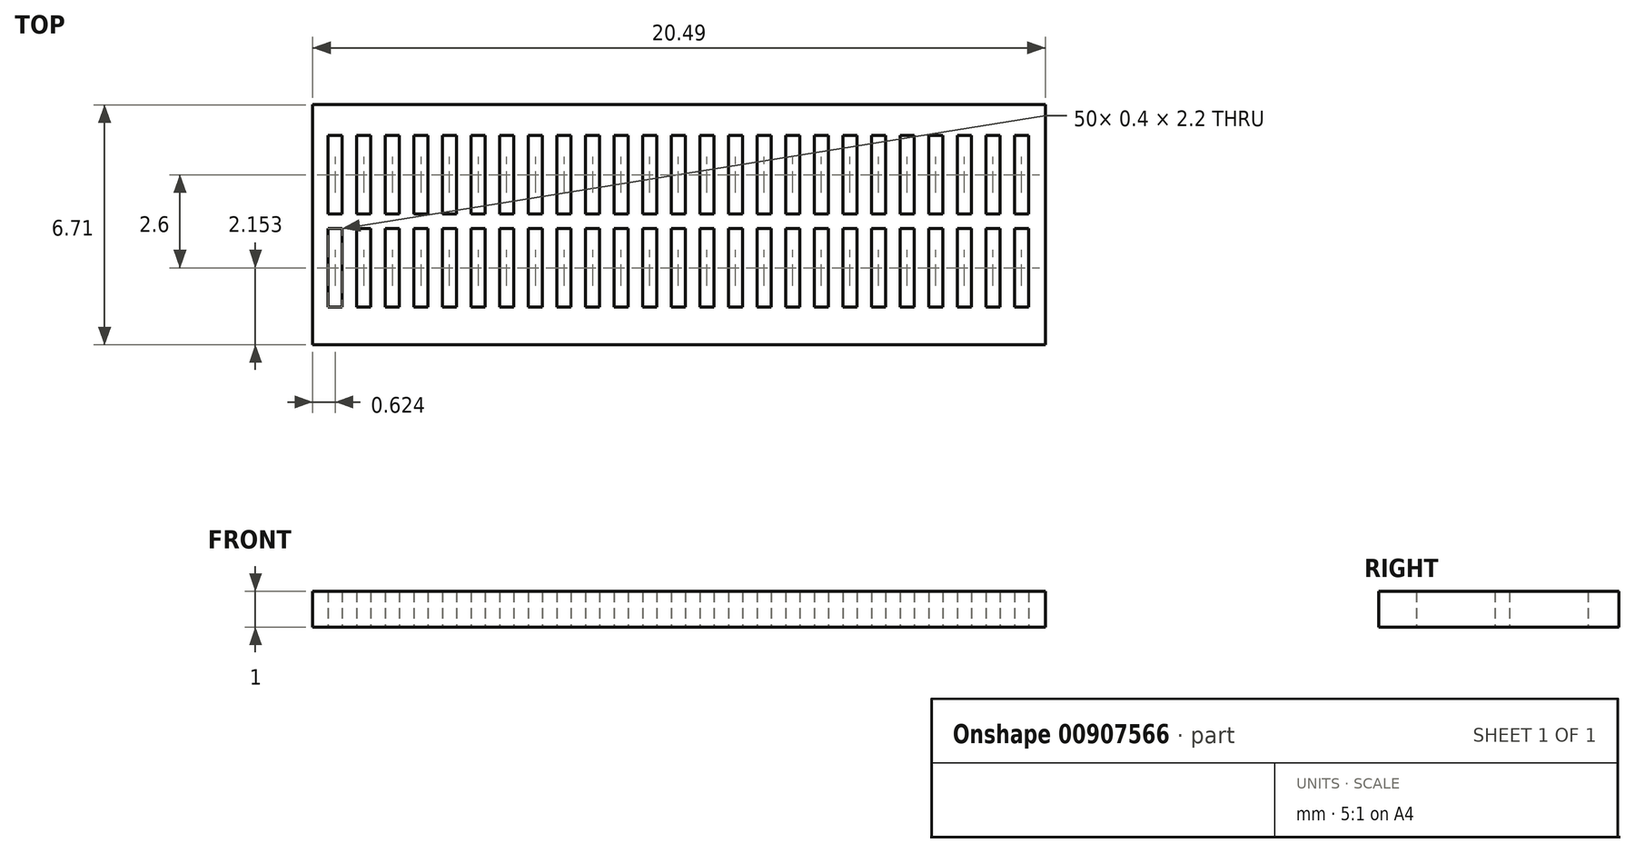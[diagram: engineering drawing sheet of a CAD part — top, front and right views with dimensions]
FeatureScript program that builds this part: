
annotation { "Feature Type Name" : "Feature", "Feature Type Description" : "" }
export const myFeature = defineFeature(function(context is Context, id is Id, definition is map)
    precondition{}
    {
        {
            var Q0;
            Q0=qCreatedBy(makeId("Top.planeOp"),FACE);
            var sketch = newSketch(context, id + "F0", { "sketchPlane" : qUnion([Q0])});
            skLineSegment(sketch, "E0.bottom", {"start": v(-8.03, 0) * mm, "end": v(-7.53, 0) * mm});
            skLineSegment(sketch, "E0.top", {"start": v(-8.03, 2.2) * mm, "end": v(-7.53, 2.2) * mm});
            skLineSegment(sketch, "E0.left", {"start": v(-8.03, 0) * mm, "end": v(-8.03, 2.2) * mm});
            skLineSegment(sketch, "E0.right", {"start": v(-7.53, 0) * mm, "end": v(-7.53, 2.2) * mm});
            skLineSegment(sketch, "E1.0.1.0", {"start": v(-8.03, -4.6) * mm, "end": v(-8.03, -2.4) * mm});
            skLineSegment(sketch, "E1.0.1.1", {"start": v(-8.03, -2.4) * mm, "end": v(-7.53, -2.4) * mm});
            skLineSegment(sketch, "E1.0.1.2", {"start": v(-7.53, -4.6) * mm, "end": v(-7.53, -2.4) * mm});
            skLineSegment(sketch, "E1.0.1.3", {"start": v(-8.03, -4.6) * mm, "end": v(-7.53, -4.6) * mm});
            skLineSegment(sketch, "E1.1.0.0", {"start": v(-7.23, 0) * mm, "end": v(-7.23, 2.2) * mm});
            skLineSegment(sketch, "E1.1.0.1", {"start": v(-7.23, 2.2) * mm, "end": v(-6.73, 2.2) * mm});
            skLineSegment(sketch, "E1.1.0.2", {"start": v(-6.73, 0) * mm, "end": v(-6.73, 2.2) * mm});
            skLineSegment(sketch, "E1.1.0.3", {"start": v(-7.23, 0) * mm, "end": v(-6.73, 0) * mm});
            skLineSegment(sketch, "E1.1.1.0", {"start": v(-7.23, -4.6) * mm, "end": v(-7.23, -2.4) * mm});
            skLineSegment(sketch, "E1.1.1.1", {"start": v(-7.23, -2.4) * mm, "end": v(-6.73, -2.4) * mm});
            skLineSegment(sketch, "E1.1.1.2", {"start": v(-6.73, -4.6) * mm, "end": v(-6.73, -2.4) * mm});
            skLineSegment(sketch, "E1.1.1.3", {"start": v(-7.23, -4.6) * mm, "end": v(-6.73, -4.6) * mm});
            skLineSegment(sketch, "E1.2.0.0", {"start": v(-6.43, 0) * mm, "end": v(-6.43, 2.2) * mm});
            skLineSegment(sketch, "E1.2.0.1", {"start": v(-6.43, 2.2) * mm, "end": v(-5.93, 2.2) * mm});
            skLineSegment(sketch, "E1.2.0.2", {"start": v(-5.93, 0) * mm, "end": v(-5.93, 2.2) * mm});
            skLineSegment(sketch, "E1.2.0.3", {"start": v(-6.43, 0) * mm, "end": v(-5.93, 0) * mm});
            skLineSegment(sketch, "E1.2.1.0", {"start": v(-6.43, -4.6) * mm, "end": v(-6.43, -2.4) * mm});
            skLineSegment(sketch, "E1.2.1.1", {"start": v(-6.43, -2.4) * mm, "end": v(-5.93, -2.4) * mm});
            skLineSegment(sketch, "E1.2.1.2", {"start": v(-5.93, -4.6) * mm, "end": v(-5.93, -2.4) * mm});
            skLineSegment(sketch, "E1.2.1.3", {"start": v(-6.43, -4.6) * mm, "end": v(-5.93, -4.6) * mm});
            skLineSegment(sketch, "E1.3.0.0", {"start": v(-5.63, 0) * mm, "end": v(-5.63, 2.2) * mm});
            skLineSegment(sketch, "E1.3.0.1", {"start": v(-5.63, 2.2) * mm, "end": v(-5.13, 2.2) * mm});
            skLineSegment(sketch, "E1.3.0.2", {"start": v(-5.13, 0) * mm, "end": v(-5.13, 2.2) * mm});
            skLineSegment(sketch, "E1.3.0.3", {"start": v(-5.63, 0) * mm, "end": v(-5.13, 0) * mm});
            skLineSegment(sketch, "E1.3.1.0", {"start": v(-5.63, -4.6) * mm, "end": v(-5.63, -2.4) * mm});
            skLineSegment(sketch, "E1.3.1.1", {"start": v(-5.63, -2.4) * mm, "end": v(-5.13, -2.4) * mm});
            skLineSegment(sketch, "E1.3.1.2", {"start": v(-5.13, -4.6) * mm, "end": v(-5.13, -2.4) * mm});
            skLineSegment(sketch, "E1.3.1.3", {"start": v(-5.63, -4.6) * mm, "end": v(-5.13, -4.6) * mm});
            skLineSegment(sketch, "E1.4.0.0", {"start": v(-4.83, 0) * mm, "end": v(-4.83, 2.2) * mm});
            skLineSegment(sketch, "E1.4.0.1", {"start": v(-4.83, 2.2) * mm, "end": v(-4.33, 2.2) * mm});
            skLineSegment(sketch, "E1.4.0.2", {"start": v(-4.33, 0) * mm, "end": v(-4.33, 2.2) * mm});
            skLineSegment(sketch, "E1.4.0.3", {"start": v(-4.83, 0) * mm, "end": v(-4.33, 0) * mm});
            skLineSegment(sketch, "E1.4.1.0", {"start": v(-4.83, -4.6) * mm, "end": v(-4.83, -2.4) * mm});
            skLineSegment(sketch, "E1.4.1.1", {"start": v(-4.83, -2.4) * mm, "end": v(-4.33, -2.4) * mm});
            skLineSegment(sketch, "E1.4.1.2", {"start": v(-4.33, -4.6) * mm, "end": v(-4.33, -2.4) * mm});
            skLineSegment(sketch, "E1.4.1.3", {"start": v(-4.83, -4.6) * mm, "end": v(-4.33, -4.6) * mm});
            skLineSegment(sketch, "E1.5.0.0", {"start": v(-4.03, 0) * mm, "end": v(-4.03, 2.2) * mm});
            skLineSegment(sketch, "E1.5.0.1", {"start": v(-4.03, 2.2) * mm, "end": v(-3.53, 2.2) * mm});
            skLineSegment(sketch, "E1.5.0.2", {"start": v(-3.53, 0) * mm, "end": v(-3.53, 2.2) * mm});
            skLineSegment(sketch, "E1.5.0.3", {"start": v(-4.03, 0) * mm, "end": v(-3.53, 0) * mm});
            skLineSegment(sketch, "E1.5.1.0", {"start": v(-4.03, -4.6) * mm, "end": v(-4.03, -2.4) * mm});
            skLineSegment(sketch, "E1.5.1.1", {"start": v(-4.03, -2.4) * mm, "end": v(-3.53, -2.4) * mm});
            skLineSegment(sketch, "E1.5.1.2", {"start": v(-3.53, -4.6) * mm, "end": v(-3.53, -2.4) * mm});
            skLineSegment(sketch, "E1.5.1.3", {"start": v(-4.03, -4.6) * mm, "end": v(-3.53, -4.6) * mm});
            skLineSegment(sketch, "E1.6.0.0", {"start": v(-3.23, 0) * mm, "end": v(-3.23, 2.2) * mm});
            skLineSegment(sketch, "E1.6.0.1", {"start": v(-3.23, 2.2) * mm, "end": v(-2.73, 2.2) * mm});
            skLineSegment(sketch, "E1.6.0.2", {"start": v(-2.73, 0) * mm, "end": v(-2.73, 2.2) * mm});
            skLineSegment(sketch, "E1.6.0.3", {"start": v(-3.23, 0) * mm, "end": v(-2.73, 0) * mm});
            skLineSegment(sketch, "E1.6.1.0", {"start": v(-3.23, -4.6) * mm, "end": v(-3.23, -2.4) * mm});
            skLineSegment(sketch, "E1.6.1.1", {"start": v(-3.23, -2.4) * mm, "end": v(-2.73, -2.4) * mm});
            skLineSegment(sketch, "E1.6.1.2", {"start": v(-2.73, -4.6) * mm, "end": v(-2.73, -2.4) * mm});
            skLineSegment(sketch, "E1.6.1.3", {"start": v(-3.23, -4.6) * mm, "end": v(-2.73, -4.6) * mm});
            skLineSegment(sketch, "E1.7.0.0", {"start": v(-2.43, 0) * mm, "end": v(-2.43, 2.2) * mm});
            skLineSegment(sketch, "E1.7.0.1", {"start": v(-2.43, 2.2) * mm, "end": v(-1.93, 2.2) * mm});
            skLineSegment(sketch, "E1.7.0.2", {"start": v(-1.93, 0) * mm, "end": v(-1.93, 2.2) * mm});
            skLineSegment(sketch, "E1.7.0.3", {"start": v(-2.43, 0) * mm, "end": v(-1.93, 0) * mm});
            skLineSegment(sketch, "E1.7.1.0", {"start": v(-2.43, -4.6) * mm, "end": v(-2.43, -2.4) * mm});
            skLineSegment(sketch, "E1.7.1.1", {"start": v(-2.43, -2.4) * mm, "end": v(-1.93, -2.4) * mm});
            skLineSegment(sketch, "E1.7.1.2", {"start": v(-1.93, -4.6) * mm, "end": v(-1.93, -2.4) * mm});
            skLineSegment(sketch, "E1.7.1.3", {"start": v(-2.43, -4.6) * mm, "end": v(-1.93, -4.6) * mm});
            skLineSegment(sketch, "E1.8.0.0", {"start": v(-1.63, 0) * mm, "end": v(-1.63, 2.2) * mm});
            skLineSegment(sketch, "E1.8.0.1", {"start": v(-1.63, 2.2) * mm, "end": v(-1.13, 2.2) * mm});
            skLineSegment(sketch, "E1.8.0.2", {"start": v(-1.13, 0) * mm, "end": v(-1.13, 2.2) * mm});
            skLineSegment(sketch, "E1.8.0.3", {"start": v(-1.63, 0) * mm, "end": v(-1.13, 0) * mm});
            skLineSegment(sketch, "E1.8.1.0", {"start": v(-1.63, -4.6) * mm, "end": v(-1.63, -2.4) * mm});
            skLineSegment(sketch, "E1.8.1.1", {"start": v(-1.63, -2.4) * mm, "end": v(-1.13, -2.4) * mm});
            skLineSegment(sketch, "E1.8.1.2", {"start": v(-1.13, -4.6) * mm, "end": v(-1.13, -2.4) * mm});
            skLineSegment(sketch, "E1.8.1.3", {"start": v(-1.63, -4.6) * mm, "end": v(-1.13, -4.6) * mm});
            skLineSegment(sketch, "E1.9.0.0", {"start": v(-0.83, 0) * mm, "end": v(-0.83, 2.2) * mm});
            skLineSegment(sketch, "E1.9.0.1", {"start": v(-0.83, 2.2) * mm, "end": v(-0.33, 2.2) * mm});
            skLineSegment(sketch, "E1.9.0.2", {"start": v(-0.33, 0) * mm, "end": v(-0.33, 2.2) * mm});
            skLineSegment(sketch, "E1.9.0.3", {"start": v(-0.83, 0) * mm, "end": v(-0.33, 0) * mm});
            skLineSegment(sketch, "E1.9.1.0", {"start": v(-0.83, -4.6) * mm, "end": v(-0.83, -2.4) * mm});
            skLineSegment(sketch, "E1.9.1.1", {"start": v(-0.83, -2.4) * mm, "end": v(-0.33, -2.4) * mm});
            skLineSegment(sketch, "E1.9.1.2", {"start": v(-0.33, -4.6) * mm, "end": v(-0.33, -2.4) * mm});
            skLineSegment(sketch, "E1.9.1.3", {"start": v(-0.83, -4.6) * mm, "end": v(-0.33, -4.6) * mm});
            skLineSegment(sketch, "E1.10.0.0", {"start": v(-0.03, 0) * mm, "end": v(-0.03, 2.2) * mm});
            skLineSegment(sketch, "E1.10.0.1", {"start": v(-0.03, 2.2) * mm, "end": v(0.47, 2.2) * mm});
            skLineSegment(sketch, "E1.10.0.2", {"start": v(0.47, 0) * mm, "end": v(0.47, 2.2) * mm});
            skLineSegment(sketch, "E1.10.0.3", {"start": v(-0.03, 0) * mm, "end": v(0.47, 0) * mm});
            skLineSegment(sketch, "E1.10.1.0", {"start": v(-0.03, -4.6) * mm, "end": v(-0.03, -2.4) * mm});
            skLineSegment(sketch, "E1.10.1.1", {"start": v(-0.03, -2.4) * mm, "end": v(0.47, -2.4) * mm});
            skLineSegment(sketch, "E1.10.1.2", {"start": v(0.47, -4.6) * mm, "end": v(0.47, -2.4) * mm});
            skLineSegment(sketch, "E1.10.1.3", {"start": v(-0.03, -4.6) * mm, "end": v(0.47, -4.6) * mm});
            skLineSegment(sketch, "E1.11.0.0", {"start": v(0.77, 0) * mm, "end": v(0.77, 2.2) * mm});
            skLineSegment(sketch, "E1.11.0.1", {"start": v(0.77, 2.2) * mm, "end": v(1.27, 2.2) * mm});
            skLineSegment(sketch, "E1.11.0.2", {"start": v(1.27, 0) * mm, "end": v(1.27, 2.2) * mm});
            skLineSegment(sketch, "E1.11.0.3", {"start": v(0.77, 0) * mm, "end": v(1.27, 0) * mm});
            skLineSegment(sketch, "E1.11.1.0", {"start": v(0.77, -4.6) * mm, "end": v(0.77, -2.4) * mm});
            skLineSegment(sketch, "E1.11.1.1", {"start": v(0.77, -2.4) * mm, "end": v(1.27, -2.4) * mm});
            skLineSegment(sketch, "E1.11.1.2", {"start": v(1.27, -4.6) * mm, "end": v(1.27, -2.4) * mm});
            skLineSegment(sketch, "E1.11.1.3", {"start": v(0.77, -4.6) * mm, "end": v(1.27, -4.6) * mm});
            skLineSegment(sketch, "E1.12.0.0", {"start": v(1.57, 0) * mm, "end": v(1.57, 2.2) * mm});
            skLineSegment(sketch, "E1.12.0.1", {"start": v(1.57, 2.2) * mm, "end": v(2.07, 2.2) * mm});
            skLineSegment(sketch, "E1.12.0.2", {"start": v(2.07, 0) * mm, "end": v(2.07, 2.2) * mm});
            skLineSegment(sketch, "E1.12.0.3", {"start": v(1.57, 0) * mm, "end": v(2.07, 0) * mm});
            skLineSegment(sketch, "E1.12.1.0", {"start": v(1.57, -4.6) * mm, "end": v(1.57, -2.4) * mm});
            skLineSegment(sketch, "E1.12.1.1", {"start": v(1.57, -2.4) * mm, "end": v(2.07, -2.4) * mm});
            skLineSegment(sketch, "E1.12.1.2", {"start": v(2.07, -4.6) * mm, "end": v(2.07, -2.4) * mm});
            skLineSegment(sketch, "E1.12.1.3", {"start": v(1.57, -4.6) * mm, "end": v(2.07, -4.6) * mm});
            skLineSegment(sketch, "E1.13.0.0", {"start": v(2.37, 0) * mm, "end": v(2.37, 2.2) * mm});
            skLineSegment(sketch, "E1.13.0.1", {"start": v(2.37, 2.2) * mm, "end": v(2.87, 2.2) * mm});
            skLineSegment(sketch, "E1.13.0.2", {"start": v(2.87, 0) * mm, "end": v(2.87, 2.2) * mm});
            skLineSegment(sketch, "E1.13.0.3", {"start": v(2.37, 0) * mm, "end": v(2.87, 0) * mm});
            skLineSegment(sketch, "E1.13.1.0", {"start": v(2.37, -4.6) * mm, "end": v(2.37, -2.4) * mm});
            skLineSegment(sketch, "E1.13.1.1", {"start": v(2.37, -2.4) * mm, "end": v(2.87, -2.4) * mm});
            skLineSegment(sketch, "E1.13.1.2", {"start": v(2.87, -4.6) * mm, "end": v(2.87, -2.4) * mm});
            skLineSegment(sketch, "E1.13.1.3", {"start": v(2.37, -4.6) * mm, "end": v(2.87, -4.6) * mm});
            skLineSegment(sketch, "E1.14.0.0", {"start": v(3.17, 0) * mm, "end": v(3.17, 2.2) * mm});
            skLineSegment(sketch, "E1.14.0.1", {"start": v(3.17, 2.2) * mm, "end": v(3.67, 2.2) * mm});
            skLineSegment(sketch, "E1.14.0.2", {"start": v(3.67, 0) * mm, "end": v(3.67, 2.2) * mm});
            skLineSegment(sketch, "E1.14.0.3", {"start": v(3.17, 0) * mm, "end": v(3.67, 0) * mm});
            skLineSegment(sketch, "E1.14.1.0", {"start": v(3.17, -4.6) * mm, "end": v(3.17, -2.4) * mm});
            skLineSegment(sketch, "E1.14.1.1", {"start": v(3.17, -2.4) * mm, "end": v(3.67, -2.4) * mm});
            skLineSegment(sketch, "E1.14.1.2", {"start": v(3.67, -4.6) * mm, "end": v(3.67, -2.4) * mm});
            skLineSegment(sketch, "E1.14.1.3", {"start": v(3.17, -4.6) * mm, "end": v(3.67, -4.6) * mm});
            skLineSegment(sketch, "E1.15.0.0", {"start": v(3.97, 0) * mm, "end": v(3.97, 2.2) * mm});
            skLineSegment(sketch, "E1.15.0.1", {"start": v(3.97, 2.2) * mm, "end": v(4.47, 2.2) * mm});
            skLineSegment(sketch, "E1.15.0.2", {"start": v(4.47, 0) * mm, "end": v(4.47, 2.2) * mm});
            skLineSegment(sketch, "E1.15.0.3", {"start": v(3.97, 0) * mm, "end": v(4.47, 0) * mm});
            skLineSegment(sketch, "E1.15.1.0", {"start": v(3.97, -4.6) * mm, "end": v(3.97, -2.4) * mm});
            skLineSegment(sketch, "E1.15.1.1", {"start": v(3.97, -2.4) * mm, "end": v(4.47, -2.4) * mm});
            skLineSegment(sketch, "E1.15.1.2", {"start": v(4.47, -4.6) * mm, "end": v(4.47, -2.4) * mm});
            skLineSegment(sketch, "E1.15.1.3", {"start": v(3.97, -4.6) * mm, "end": v(4.47, -4.6) * mm});
            skLineSegment(sketch, "E1.16.0.0", {"start": v(4.77, 0) * mm, "end": v(4.77, 2.2) * mm});
            skLineSegment(sketch, "E1.16.0.1", {"start": v(4.77, 2.2) * mm, "end": v(5.27, 2.2) * mm});
            skLineSegment(sketch, "E1.16.0.2", {"start": v(5.27, 0) * mm, "end": v(5.27, 2.2) * mm});
            skLineSegment(sketch, "E1.16.0.3", {"start": v(4.77, 0) * mm, "end": v(5.27, 0) * mm});
            skLineSegment(sketch, "E1.16.1.0", {"start": v(4.77, -4.6) * mm, "end": v(4.77, -2.4) * mm});
            skLineSegment(sketch, "E1.16.1.1", {"start": v(4.77, -2.4) * mm, "end": v(5.27, -2.4) * mm});
            skLineSegment(sketch, "E1.16.1.2", {"start": v(5.27, -4.6) * mm, "end": v(5.27, -2.4) * mm});
            skLineSegment(sketch, "E1.16.1.3", {"start": v(4.77, -4.6) * mm, "end": v(5.27, -4.6) * mm});
            skLineSegment(sketch, "E1.17.0.0", {"start": v(5.57, 0) * mm, "end": v(5.57, 2.2) * mm});
            skLineSegment(sketch, "E1.17.0.1", {"start": v(5.57, 2.2) * mm, "end": v(6.07, 2.2) * mm});
            skLineSegment(sketch, "E1.17.0.2", {"start": v(6.07, 0) * mm, "end": v(6.07, 2.2) * mm});
            skLineSegment(sketch, "E1.17.0.3", {"start": v(5.57, 0) * mm, "end": v(6.07, 0) * mm});
            skLineSegment(sketch, "E1.17.1.0", {"start": v(5.57, -4.6) * mm, "end": v(5.57, -2.4) * mm});
            skLineSegment(sketch, "E1.17.1.1", {"start": v(5.57, -2.4) * mm, "end": v(6.07, -2.4) * mm});
            skLineSegment(sketch, "E1.17.1.2", {"start": v(6.07, -4.6) * mm, "end": v(6.07, -2.4) * mm});
            skLineSegment(sketch, "E1.17.1.3", {"start": v(5.57, -4.6) * mm, "end": v(6.07, -4.6) * mm});
            skLineSegment(sketch, "E1.18.0.0", {"start": v(6.37, 0) * mm, "end": v(6.37, 2.2) * mm});
            skLineSegment(sketch, "E1.18.0.1", {"start": v(6.37, 2.2) * mm, "end": v(6.87, 2.2) * mm});
            skLineSegment(sketch, "E1.18.0.2", {"start": v(6.87, 0) * mm, "end": v(6.87, 2.2) * mm});
            skLineSegment(sketch, "E1.18.0.3", {"start": v(6.37, 0) * mm, "end": v(6.87, 0) * mm});
            skLineSegment(sketch, "E1.18.1.0", {"start": v(6.37, -4.6) * mm, "end": v(6.37, -2.4) * mm});
            skLineSegment(sketch, "E1.18.1.1", {"start": v(6.37, -2.4) * mm, "end": v(6.87, -2.4) * mm});
            skLineSegment(sketch, "E1.18.1.2", {"start": v(6.87, -4.6) * mm, "end": v(6.87, -2.4) * mm});
            skLineSegment(sketch, "E1.18.1.3", {"start": v(6.37, -4.6) * mm, "end": v(6.87, -4.6) * mm});
            skLineSegment(sketch, "E1.19.0.0", {"start": v(7.17, 0) * mm, "end": v(7.17, 2.2) * mm});
            skLineSegment(sketch, "E1.19.0.1", {"start": v(7.17, 2.2) * mm, "end": v(7.67, 2.2) * mm});
            skLineSegment(sketch, "E1.19.0.2", {"start": v(7.67, 0) * mm, "end": v(7.67, 2.2) * mm});
            skLineSegment(sketch, "E1.19.0.3", {"start": v(7.17, 0) * mm, "end": v(7.67, 0) * mm});
            skLineSegment(sketch, "E1.19.1.0", {"start": v(7.17, -4.6) * mm, "end": v(7.17, -2.4) * mm});
            skLineSegment(sketch, "E1.19.1.1", {"start": v(7.17, -2.4) * mm, "end": v(7.67, -2.4) * mm});
            skLineSegment(sketch, "E1.19.1.2", {"start": v(7.67, -4.6) * mm, "end": v(7.67, -2.4) * mm});
            skLineSegment(sketch, "E1.19.1.3", {"start": v(7.17, -4.6) * mm, "end": v(7.67, -4.6) * mm});
            skLineSegment(sketch, "E1.20.0.0", {"start": v(7.97, 0) * mm, "end": v(7.97, 2.2) * mm});
            skLineSegment(sketch, "E1.20.0.1", {"start": v(7.97, 2.2) * mm, "end": v(8.47, 2.2) * mm});
            skLineSegment(sketch, "E1.20.0.2", {"start": v(8.47, 0) * mm, "end": v(8.47, 2.2) * mm});
            skLineSegment(sketch, "E1.20.0.3", {"start": v(7.97, 0) * mm, "end": v(8.47, 0) * mm});
            skLineSegment(sketch, "E1.20.1.0", {"start": v(7.97, -4.6) * mm, "end": v(7.97, -2.4) * mm});
            skLineSegment(sketch, "E1.20.1.1", {"start": v(7.97, -2.4) * mm, "end": v(8.47, -2.4) * mm});
            skLineSegment(sketch, "E1.20.1.2", {"start": v(8.47, -4.6) * mm, "end": v(8.47, -2.4) * mm});
            skLineSegment(sketch, "E1.20.1.3", {"start": v(7.97, -4.6) * mm, "end": v(8.47, -4.6) * mm});
            skLineSegment(sketch, "E1.21.0.0", {"start": v(8.77, 0) * mm, "end": v(8.77, 2.2) * mm});
            skLineSegment(sketch, "E1.21.0.1", {"start": v(8.77, 2.2) * mm, "end": v(9.27, 2.2) * mm});
            skLineSegment(sketch, "E1.21.0.2", {"start": v(9.27, 0) * mm, "end": v(9.27, 2.2) * mm});
            skLineSegment(sketch, "E1.21.0.3", {"start": v(8.77, 0) * mm, "end": v(9.27, 0) * mm});
            skLineSegment(sketch, "E1.21.1.0", {"start": v(8.77, -4.6) * mm, "end": v(8.77, -2.4) * mm});
            skLineSegment(sketch, "E1.21.1.1", {"start": v(8.77, -2.4) * mm, "end": v(9.27, -2.4) * mm});
            skLineSegment(sketch, "E1.21.1.2", {"start": v(9.27, -4.6) * mm, "end": v(9.27, -2.4) * mm});
            skLineSegment(sketch, "E1.21.1.3", {"start": v(8.77, -4.6) * mm, "end": v(9.27, -4.6) * mm});
            skLineSegment(sketch, "E1.22.0.0", {"start": v(9.57, 0) * mm, "end": v(9.57, 2.2) * mm});
            skLineSegment(sketch, "E1.22.0.1", {"start": v(9.57, 2.2) * mm, "end": v(10.07, 2.2) * mm});
            skLineSegment(sketch, "E1.22.0.2", {"start": v(10.07, 0) * mm, "end": v(10.07, 2.2) * mm});
            skLineSegment(sketch, "E1.22.0.3", {"start": v(9.57, 0) * mm, "end": v(10.07, 0) * mm});
            skLineSegment(sketch, "E1.22.1.0", {"start": v(9.57, -4.6) * mm, "end": v(9.57, -2.4) * mm});
            skLineSegment(sketch, "E1.22.1.1", {"start": v(9.57, -2.4) * mm, "end": v(10.07, -2.4) * mm});
            skLineSegment(sketch, "E1.22.1.2", {"start": v(10.07, -4.6) * mm, "end": v(10.07, -2.4) * mm});
            skLineSegment(sketch, "E1.22.1.3", {"start": v(9.57, -4.6) * mm, "end": v(10.07, -4.6) * mm});
            skLineSegment(sketch, "E1.23.0.0", {"start": v(10.37, 0) * mm, "end": v(10.37, 2.2) * mm});
            skLineSegment(sketch, "E1.23.0.1", {"start": v(10.37, 2.2) * mm, "end": v(10.87, 2.2) * mm});
            skLineSegment(sketch, "E1.23.0.2", {"start": v(10.87, 0) * mm, "end": v(10.87, 2.2) * mm});
            skLineSegment(sketch, "E1.23.0.3", {"start": v(10.37, 0) * mm, "end": v(10.87, 0) * mm});
            skLineSegment(sketch, "E1.23.1.0", {"start": v(10.37, -4.6) * mm, "end": v(10.37, -2.4) * mm});
            skLineSegment(sketch, "E1.23.1.1", {"start": v(10.37, -2.4) * mm, "end": v(10.87, -2.4) * mm});
            skLineSegment(sketch, "E1.23.1.2", {"start": v(10.87, -4.6) * mm, "end": v(10.87, -2.4) * mm});
            skLineSegment(sketch, "E1.23.1.3", {"start": v(10.37, -4.6) * mm, "end": v(10.87, -4.6) * mm});
            skLineSegment(sketch, "E1.24.0.0", {"start": v(11.17, 0) * mm, "end": v(11.17, 2.2) * mm});
            skLineSegment(sketch, "E1.24.0.1", {"start": v(11.17, 2.2) * mm, "end": v(11.67, 2.2) * mm});
            skLineSegment(sketch, "E1.24.0.2", {"start": v(11.67, 0) * mm, "end": v(11.67, 2.2) * mm});
            skLineSegment(sketch, "E1.24.0.3", {"start": v(11.17, 0) * mm, "end": v(11.67, 0) * mm});
            skLineSegment(sketch, "E1.24.1.0", {"start": v(11.17, -4.6) * mm, "end": v(11.17, -2.4) * mm});
            skLineSegment(sketch, "E1.24.1.1", {"start": v(11.17, -2.4) * mm, "end": v(11.67, -2.4) * mm});
            skLineSegment(sketch, "E1.24.1.2", {"start": v(11.67, -4.6) * mm, "end": v(11.67, -2.4) * mm});
            skLineSegment(sketch, "E1.24.1.3", {"start": v(11.17, -4.6) * mm, "end": v(11.67, -4.6) * mm});
            skLineSegment(sketch, "E1.25.0.0", {"start": v(11.97, 0) * mm, "end": v(11.97, 2.2) * mm});
            skLineSegment(sketch, "E1.25.0.1", {"start": v(11.97, 2.2) * mm, "end": v(12.47, 2.2) * mm});
            skLineSegment(sketch, "E1.25.0.2", {"start": v(12.47, 0) * mm, "end": v(12.47, 2.2) * mm});
            skLineSegment(sketch, "E1.25.0.3", {"start": v(11.97, 0) * mm, "end": v(12.47, 0) * mm});
            skLineSegment(sketch, "E1.25.1.0", {"start": v(11.97, -4.6) * mm, "end": v(11.97, -2.4) * mm});
            skLineSegment(sketch, "E1.25.1.1", {"start": v(11.97, -2.4) * mm, "end": v(12.47, -2.4) * mm});
            skLineSegment(sketch, "E1.25.1.2", {"start": v(12.47, -4.6) * mm, "end": v(12.47, -2.4) * mm});
            skLineSegment(sketch, "E1.25.1.3", {"start": v(11.97, -4.6) * mm, "end": v(12.47, -4.6) * mm});
            skLineSegment(sketch, "E1.26.0.0", {"start": v(12.77, 0) * mm, "end": v(12.77, 2.2) * mm});
            skLineSegment(sketch, "E1.26.0.1", {"start": v(12.77, 2.2) * mm, "end": v(13.27, 2.2) * mm});
            skLineSegment(sketch, "E1.26.0.2", {"start": v(13.27, 0) * mm, "end": v(13.27, 2.2) * mm});
            skLineSegment(sketch, "E1.26.0.3", {"start": v(12.77, 0) * mm, "end": v(13.27, 0) * mm});
            skLineSegment(sketch, "E1.26.1.0", {"start": v(12.77, -4.6) * mm, "end": v(12.77, -2.4) * mm});
            skLineSegment(sketch, "E1.26.1.1", {"start": v(12.77, -2.4) * mm, "end": v(13.27, -2.4) * mm});
            skLineSegment(sketch, "E1.26.1.2", {"start": v(13.27, -4.6) * mm, "end": v(13.27, -2.4) * mm});
            skLineSegment(sketch, "E1.26.1.3", {"start": v(12.77, -4.6) * mm, "end": v(13.27, -4.6) * mm});
            skLineSegment(sketch, "E1.27.0.0", {"start": v(13.57, 0) * mm, "end": v(13.57, 2.2) * mm});
            skLineSegment(sketch, "E1.27.0.1", {"start": v(13.57, 2.2) * mm, "end": v(14.07, 2.2) * mm});
            skLineSegment(sketch, "E1.27.0.2", {"start": v(14.07, 0) * mm, "end": v(14.07, 2.2) * mm});
            skLineSegment(sketch, "E1.27.0.3", {"start": v(13.57, 0) * mm, "end": v(14.07, 0) * mm});
            skLineSegment(sketch, "E1.27.1.0", {"start": v(13.57, -4.6) * mm, "end": v(13.57, -2.4) * mm});
            skLineSegment(sketch, "E1.27.1.1", {"start": v(13.57, -2.4) * mm, "end": v(14.07, -2.4) * mm});
            skLineSegment(sketch, "E1.27.1.2", {"start": v(14.07, -4.6) * mm, "end": v(14.07, -2.4) * mm});
            skLineSegment(sketch, "E1.27.1.3", {"start": v(13.57, -4.6) * mm, "end": v(14.07, -4.6) * mm});
            skLineSegment(sketch, "E1.28.0.0", {"start": v(14.37, 0) * mm, "end": v(14.37, 2.2) * mm});
            skLineSegment(sketch, "E1.28.0.1", {"start": v(14.37, 2.2) * mm, "end": v(14.87, 2.2) * mm});
            skLineSegment(sketch, "E1.28.0.2", {"start": v(14.87, 0) * mm, "end": v(14.87, 2.2) * mm});
            skLineSegment(sketch, "E1.28.0.3", {"start": v(14.37, 0) * mm, "end": v(14.87, 0) * mm});
            skLineSegment(sketch, "E1.28.1.0", {"start": v(14.37, -4.6) * mm, "end": v(14.37, -2.4) * mm});
            skLineSegment(sketch, "E1.28.1.1", {"start": v(14.37, -2.4) * mm, "end": v(14.87, -2.4) * mm});
            skLineSegment(sketch, "E1.28.1.2", {"start": v(14.87, -4.6) * mm, "end": v(14.87, -2.4) * mm});
            skLineSegment(sketch, "E1.28.1.3", {"start": v(14.37, -4.6) * mm, "end": v(14.87, -4.6) * mm});
            skLineSegment(sketch, "E1.29.0.0", {"start": v(15.17, 0) * mm, "end": v(15.17, 2.2) * mm});
            skLineSegment(sketch, "E1.29.0.1", {"start": v(15.17, 2.2) * mm, "end": v(15.67, 2.2) * mm});
            skLineSegment(sketch, "E1.29.0.2", {"start": v(15.67, 0) * mm, "end": v(15.67, 2.2) * mm});
            skLineSegment(sketch, "E1.29.0.3", {"start": v(15.17, 0) * mm, "end": v(15.67, 0) * mm});
            skLineSegment(sketch, "E1.29.1.0", {"start": v(15.17, -4.6) * mm, "end": v(15.17, -2.4) * mm});
            skLineSegment(sketch, "E1.29.1.1", {"start": v(15.17, -2.4) * mm, "end": v(15.67, -2.4) * mm});
            skLineSegment(sketch, "E1.29.1.2", {"start": v(15.67, -4.6) * mm, "end": v(15.67, -2.4) * mm});
            skLineSegment(sketch, "E1.29.1.3", {"start": v(15.17, -4.6) * mm, "end": v(15.67, -4.6) * mm});
            skLineSegment(sketch, "E1.30.0.0", {"start": v(15.97, 0) * mm, "end": v(15.97, 2.2) * mm});
            skLineSegment(sketch, "E1.30.0.1", {"start": v(15.97, 2.2) * mm, "end": v(16.47, 2.2) * mm});
            skLineSegment(sketch, "E1.30.0.2", {"start": v(16.47, 0) * mm, "end": v(16.47, 2.2) * mm});
            skLineSegment(sketch, "E1.30.0.3", {"start": v(15.97, 0) * mm, "end": v(16.47, 0) * mm});
            skLineSegment(sketch, "E1.30.1.0", {"start": v(15.97, -4.6) * mm, "end": v(15.97, -2.4) * mm});
            skLineSegment(sketch, "E1.30.1.1", {"start": v(15.97, -2.4) * mm, "end": v(16.47, -2.4) * mm});
            skLineSegment(sketch, "E1.30.1.2", {"start": v(16.47, -4.6) * mm, "end": v(16.47, -2.4) * mm});
            skLineSegment(sketch, "E1.30.1.3", {"start": v(15.97, -4.6) * mm, "end": v(16.47, -4.6) * mm});
            skLineSegment(sketch, "E1.31.0.0", {"start": v(16.77, 0) * mm, "end": v(16.77, 2.2) * mm});
            skLineSegment(sketch, "E1.31.0.1", {"start": v(16.77, 2.2) * mm, "end": v(17.27, 2.2) * mm});
            skLineSegment(sketch, "E1.31.0.2", {"start": v(17.27, 0) * mm, "end": v(17.27, 2.2) * mm});
            skLineSegment(sketch, "E1.31.0.3", {"start": v(16.77, 0) * mm, "end": v(17.27, 0) * mm});
            skLineSegment(sketch, "E1.31.1.0", {"start": v(16.77, -4.6) * mm, "end": v(16.77, -2.4) * mm});
            skLineSegment(sketch, "E1.31.1.1", {"start": v(16.77, -2.4) * mm, "end": v(17.27, -2.4) * mm});
            skLineSegment(sketch, "E1.31.1.2", {"start": v(17.27, -4.6) * mm, "end": v(17.27, -2.4) * mm});
            skLineSegment(sketch, "E1.31.1.3", {"start": v(16.77, -4.6) * mm, "end": v(17.27, -4.6) * mm});
            skLineSegment(sketch, "E1.32.0.0", {"start": v(17.57, 0) * mm, "end": v(17.57, 2.2) * mm});
            skLineSegment(sketch, "E1.32.0.1", {"start": v(17.57, 2.2) * mm, "end": v(18.07, 2.2) * mm});
            skLineSegment(sketch, "E1.32.0.2", {"start": v(18.07, 0) * mm, "end": v(18.07, 2.2) * mm});
            skLineSegment(sketch, "E1.32.0.3", {"start": v(17.57, 0) * mm, "end": v(18.07, 0) * mm});
            skLineSegment(sketch, "E1.32.1.0", {"start": v(17.57, -4.6) * mm, "end": v(17.57, -2.4) * mm});
            skLineSegment(sketch, "E1.32.1.1", {"start": v(17.57, -2.4) * mm, "end": v(18.07, -2.4) * mm});
            skLineSegment(sketch, "E1.32.1.2", {"start": v(18.07, -4.6) * mm, "end": v(18.07, -2.4) * mm});
            skLineSegment(sketch, "E1.32.1.3", {"start": v(17.57, -4.6) * mm, "end": v(18.07, -4.6) * mm});
            skLineSegment(sketch, "E1.33.0.0", {"start": v(18.37, 0) * mm, "end": v(18.37, 2.2) * mm});
            skLineSegment(sketch, "E1.33.0.1", {"start": v(18.37, 2.2) * mm, "end": v(18.87, 2.2) * mm});
            skLineSegment(sketch, "E1.33.0.2", {"start": v(18.87, 0) * mm, "end": v(18.87, 2.2) * mm});
            skLineSegment(sketch, "E1.33.0.3", {"start": v(18.37, 0) * mm, "end": v(18.87, 0) * mm});
            skLineSegment(sketch, "E1.33.1.0", {"start": v(18.37, -4.6) * mm, "end": v(18.37, -2.4) * mm});
            skLineSegment(sketch, "E1.33.1.1", {"start": v(18.37, -2.4) * mm, "end": v(18.87, -2.4) * mm});
            skLineSegment(sketch, "E1.33.1.2", {"start": v(18.87, -4.6) * mm, "end": v(18.87, -2.4) * mm});
            skLineSegment(sketch, "E1.33.1.3", {"start": v(18.37, -4.6) * mm, "end": v(18.87, -4.6) * mm});
            skLineSegment(sketch, "E1.34.0.0", {"start": v(19.17, 0) * mm, "end": v(19.17, 2.2) * mm});
            skLineSegment(sketch, "E1.34.0.1", {"start": v(19.17, 2.2) * mm, "end": v(19.67, 2.2) * mm});
            skLineSegment(sketch, "E1.34.0.2", {"start": v(19.67, 0) * mm, "end": v(19.67, 2.2) * mm});
            skLineSegment(sketch, "E1.34.0.3", {"start": v(19.17, 0) * mm, "end": v(19.67, 0) * mm});
            skLineSegment(sketch, "E1.34.1.0", {"start": v(19.17, -4.6) * mm, "end": v(19.17, -2.4) * mm});
            skLineSegment(sketch, "E1.34.1.1", {"start": v(19.17, -2.4) * mm, "end": v(19.67, -2.4) * mm});
            skLineSegment(sketch, "E1.34.1.2", {"start": v(19.67, -4.6) * mm, "end": v(19.67, -2.4) * mm});
            skLineSegment(sketch, "E1.34.1.3", {"start": v(19.17, -4.6) * mm, "end": v(19.67, -4.6) * mm});
            skLineSegment(sketch, "E1.35.0.0", {"start": v(19.97, 0) * mm, "end": v(19.97, 2.2) * mm});
            skLineSegment(sketch, "E1.35.0.1", {"start": v(19.97, 2.2) * mm, "end": v(20.47, 2.2) * mm});
            skLineSegment(sketch, "E1.35.0.2", {"start": v(20.47, 0) * mm, "end": v(20.47, 2.2) * mm});
            skLineSegment(sketch, "E1.35.0.3", {"start": v(19.97, 0) * mm, "end": v(20.47, 0) * mm});
            skLineSegment(sketch, "E1.35.1.0", {"start": v(19.97, -4.6) * mm, "end": v(19.97, -2.4) * mm});
            skLineSegment(sketch, "E1.35.1.1", {"start": v(19.97, -2.4) * mm, "end": v(20.47, -2.4) * mm});
            skLineSegment(sketch, "E1.35.1.2", {"start": v(20.47, -4.6) * mm, "end": v(20.47, -2.4) * mm});
            skLineSegment(sketch, "E1.35.1.3", {"start": v(19.97, -4.6) * mm, "end": v(20.47, -4.6) * mm});
            skLineSegment(sketch, "E1.36.0.0", {"start": v(20.77, 0) * mm, "end": v(20.77, 2.2) * mm});
            skLineSegment(sketch, "E1.36.0.1", {"start": v(20.77, 2.2) * mm, "end": v(21.27, 2.2) * mm});
            skLineSegment(sketch, "E1.36.0.2", {"start": v(21.27, 0) * mm, "end": v(21.27, 2.2) * mm});
            skLineSegment(sketch, "E1.36.0.3", {"start": v(20.77, 0) * mm, "end": v(21.27, 0) * mm});
            skLineSegment(sketch, "E1.36.1.0", {"start": v(20.77, -4.6) * mm, "end": v(20.77, -2.4) * mm});
            skLineSegment(sketch, "E1.36.1.1", {"start": v(20.77, -2.4) * mm, "end": v(21.27, -2.4) * mm});
            skLineSegment(sketch, "E1.36.1.2", {"start": v(21.27, -4.6) * mm, "end": v(21.27, -2.4) * mm});
            skLineSegment(sketch, "E1.36.1.3", {"start": v(20.77, -4.6) * mm, "end": v(21.27, -4.6) * mm});
            skLineSegment(sketch, "E1.37.0.0", {"start": v(21.57, 0) * mm, "end": v(21.57, 2.2) * mm});
            skLineSegment(sketch, "E1.37.0.1", {"start": v(21.57, 2.2) * mm, "end": v(22.07, 2.2) * mm});
            skLineSegment(sketch, "E1.37.0.2", {"start": v(22.07, 0) * mm, "end": v(22.07, 2.2) * mm});
            skLineSegment(sketch, "E1.37.0.3", {"start": v(21.57, 0) * mm, "end": v(22.07, 0) * mm});
            skLineSegment(sketch, "E1.37.1.0", {"start": v(21.57, -4.6) * mm, "end": v(21.57, -2.4) * mm});
            skLineSegment(sketch, "E1.37.1.1", {"start": v(21.57, -2.4) * mm, "end": v(22.07, -2.4) * mm});
            skLineSegment(sketch, "E1.37.1.2", {"start": v(22.07, -4.6) * mm, "end": v(22.07, -2.4) * mm});
            skLineSegment(sketch, "E1.37.1.3", {"start": v(21.57, -4.6) * mm, "end": v(22.07, -4.6) * mm});
            skLineSegment(sketch, "E1.38.0.0", {"start": v(22.37, 0) * mm, "end": v(22.37, 2.2) * mm});
            skLineSegment(sketch, "E1.38.0.1", {"start": v(22.37, 2.2) * mm, "end": v(22.87, 2.2) * mm});
            skLineSegment(sketch, "E1.38.0.2", {"start": v(22.87, 0) * mm, "end": v(22.87, 2.2) * mm});
            skLineSegment(sketch, "E1.38.0.3", {"start": v(22.37, 0) * mm, "end": v(22.87, 0) * mm});
            skLineSegment(sketch, "E1.38.1.0", {"start": v(22.37, -4.6) * mm, "end": v(22.37, -2.4) * mm});
            skLineSegment(sketch, "E1.38.1.1", {"start": v(22.37, -2.4) * mm, "end": v(22.87, -2.4) * mm});
            skLineSegment(sketch, "E1.38.1.2", {"start": v(22.87, -4.6) * mm, "end": v(22.87, -2.4) * mm});
            skLineSegment(sketch, "E1.38.1.3", {"start": v(22.37, -4.6) * mm, "end": v(22.87, -4.6) * mm});
            skLineSegment(sketch, "E1.39.0.0", {"start": v(23.17, 0) * mm, "end": v(23.17, 2.2) * mm});
            skLineSegment(sketch, "E1.39.0.1", {"start": v(23.17, 2.2) * mm, "end": v(23.67, 2.2) * mm});
            skLineSegment(sketch, "E1.39.0.2", {"start": v(23.67, 0) * mm, "end": v(23.67, 2.2) * mm});
            skLineSegment(sketch, "E1.39.0.3", {"start": v(23.17, 0) * mm, "end": v(23.67, 0) * mm});
            skLineSegment(sketch, "E1.39.1.0", {"start": v(23.17, -4.6) * mm, "end": v(23.17, -2.4) * mm});
            skLineSegment(sketch, "E1.39.1.1", {"start": v(23.17, -2.4) * mm, "end": v(23.67, -2.4) * mm});
            skLineSegment(sketch, "E1.39.1.2", {"start": v(23.67, -4.6) * mm, "end": v(23.67, -2.4) * mm});
            skLineSegment(sketch, "E1.39.1.3", {"start": v(23.17, -4.6) * mm, "end": v(23.67, -4.6) * mm});
            skLineSegment(sketch, "E1.40.0.0", {"start": v(23.97, 0) * mm, "end": v(23.97, 2.2) * mm});
            skLineSegment(sketch, "E1.40.0.1", {"start": v(23.97, 2.2) * mm, "end": v(24.47, 2.2) * mm});
            skLineSegment(sketch, "E1.40.0.2", {"start": v(24.47, 0) * mm, "end": v(24.47, 2.2) * mm});
            skLineSegment(sketch, "E1.40.0.3", {"start": v(23.97, 0) * mm, "end": v(24.47, 0) * mm});
            skLineSegment(sketch, "E1.40.1.0", {"start": v(23.97, -4.6) * mm, "end": v(23.97, -2.4) * mm});
            skLineSegment(sketch, "E1.40.1.1", {"start": v(23.97, -2.4) * mm, "end": v(24.47, -2.4) * mm});
            skLineSegment(sketch, "E1.40.1.2", {"start": v(24.47, -4.6) * mm, "end": v(24.47, -2.4) * mm});
            skLineSegment(sketch, "E1.40.1.3", {"start": v(23.97, -4.6) * mm, "end": v(24.47, -4.6) * mm});
            skLineSegment(sketch, "E1.41.0.0", {"start": v(24.77, 0) * mm, "end": v(24.77, 2.2) * mm});
            skLineSegment(sketch, "E1.41.0.1", {"start": v(24.77, 2.2) * mm, "end": v(25.27, 2.2) * mm});
            skLineSegment(sketch, "E1.41.0.2", {"start": v(25.27, 0) * mm, "end": v(25.27, 2.2) * mm});
            skLineSegment(sketch, "E1.41.0.3", {"start": v(24.77, 0) * mm, "end": v(25.27, 0) * mm});
            skLineSegment(sketch, "E1.41.1.0", {"start": v(24.77, -4.6) * mm, "end": v(24.77, -2.4) * mm});
            skLineSegment(sketch, "E1.41.1.1", {"start": v(24.77, -2.4) * mm, "end": v(25.27, -2.4) * mm});
            skLineSegment(sketch, "E1.41.1.2", {"start": v(25.27, -4.6) * mm, "end": v(25.27, -2.4) * mm});
            skLineSegment(sketch, "E1.41.1.3", {"start": v(24.77, -4.6) * mm, "end": v(25.27, -4.6) * mm});
            skLineSegment(sketch, "E1.42.0.0", {"start": v(25.57, 0) * mm, "end": v(25.57, 2.2) * mm});
            skLineSegment(sketch, "E1.42.0.1", {"start": v(25.57, 2.2) * mm, "end": v(26.07, 2.2) * mm});
            skLineSegment(sketch, "E1.42.0.2", {"start": v(26.07, 0) * mm, "end": v(26.07, 2.2) * mm});
            skLineSegment(sketch, "E1.42.0.3", {"start": v(25.57, 0) * mm, "end": v(26.07, 0) * mm});
            skLineSegment(sketch, "E1.42.1.0", {"start": v(25.57, -4.6) * mm, "end": v(25.57, -2.4) * mm});
            skLineSegment(sketch, "E1.42.1.1", {"start": v(25.57, -2.4) * mm, "end": v(26.07, -2.4) * mm});
            skLineSegment(sketch, "E1.42.1.2", {"start": v(26.07, -4.6) * mm, "end": v(26.07, -2.4) * mm});
            skLineSegment(sketch, "E1.42.1.3", {"start": v(25.57, -4.6) * mm, "end": v(26.07, -4.6) * mm});
            skLineSegment(sketch, "E1.43.0.0", {"start": v(26.37, 0) * mm, "end": v(26.37, 2.2) * mm});
            skLineSegment(sketch, "E1.43.0.1", {"start": v(26.37, 2.2) * mm, "end": v(26.87, 2.2) * mm});
            skLineSegment(sketch, "E1.43.0.2", {"start": v(26.87, 0) * mm, "end": v(26.87, 2.2) * mm});
            skLineSegment(sketch, "E1.43.0.3", {"start": v(26.37, 0) * mm, "end": v(26.87, 0) * mm});
            skLineSegment(sketch, "E1.43.1.0", {"start": v(26.37, -4.6) * mm, "end": v(26.37, -2.4) * mm});
            skLineSegment(sketch, "E1.43.1.1", {"start": v(26.37, -2.4) * mm, "end": v(26.87, -2.4) * mm});
            skLineSegment(sketch, "E1.43.1.2", {"start": v(26.87, -4.6) * mm, "end": v(26.87, -2.4) * mm});
            skLineSegment(sketch, "E1.43.1.3", {"start": v(26.37, -4.6) * mm, "end": v(26.87, -4.6) * mm});
            skLineSegment(sketch, "E1.44.0.0", {"start": v(27.17, 0) * mm, "end": v(27.17, 2.2) * mm});
            skLineSegment(sketch, "E1.44.0.1", {"start": v(27.17, 2.2) * mm, "end": v(27.67, 2.2) * mm});
            skLineSegment(sketch, "E1.44.0.2", {"start": v(27.67, 0) * mm, "end": v(27.67, 2.2) * mm});
            skLineSegment(sketch, "E1.44.0.3", {"start": v(27.17, 0) * mm, "end": v(27.67, 0) * mm});
            skLineSegment(sketch, "E1.44.1.0", {"start": v(27.17, -4.6) * mm, "end": v(27.17, -2.4) * mm});
            skLineSegment(sketch, "E1.44.1.1", {"start": v(27.17, -2.4) * mm, "end": v(27.67, -2.4) * mm});
            skLineSegment(sketch, "E1.44.1.2", {"start": v(27.67, -4.6) * mm, "end": v(27.67, -2.4) * mm});
            skLineSegment(sketch, "E1.44.1.3", {"start": v(27.17, -4.6) * mm, "end": v(27.67, -4.6) * mm});
            skLineSegment(sketch, "E1.45.0.0", {"start": v(27.97, 0) * mm, "end": v(27.97, 2.2) * mm});
            skLineSegment(sketch, "E1.45.0.1", {"start": v(27.97, 2.2) * mm, "end": v(28.47, 2.2) * mm});
            skLineSegment(sketch, "E1.45.0.2", {"start": v(28.47, 0) * mm, "end": v(28.47, 2.2) * mm});
            skLineSegment(sketch, "E1.45.0.3", {"start": v(27.97, 0) * mm, "end": v(28.47, 0) * mm});
            skLineSegment(sketch, "E1.45.1.0", {"start": v(27.97, -4.6) * mm, "end": v(27.97, -2.4) * mm});
            skLineSegment(sketch, "E1.45.1.1", {"start": v(27.97, -2.4) * mm, "end": v(28.47, -2.4) * mm});
            skLineSegment(sketch, "E1.45.1.2", {"start": v(28.47, -4.6) * mm, "end": v(28.47, -2.4) * mm});
            skLineSegment(sketch, "E1.45.1.3", {"start": v(27.97, -4.6) * mm, "end": v(28.47, -4.6) * mm});
            skLineSegment(sketch, "E1.46.0.0", {"start": v(28.77, 0) * mm, "end": v(28.77, 2.2) * mm});
            skLineSegment(sketch, "E1.46.0.1", {"start": v(28.77, 2.2) * mm, "end": v(29.27, 2.2) * mm});
            skLineSegment(sketch, "E1.46.0.2", {"start": v(29.27, 0) * mm, "end": v(29.27, 2.2) * mm});
            skLineSegment(sketch, "E1.46.0.3", {"start": v(28.77, 0) * mm, "end": v(29.27, 0) * mm});
            skLineSegment(sketch, "E1.46.1.0", {"start": v(28.77, -4.6) * mm, "end": v(28.77, -2.4) * mm});
            skLineSegment(sketch, "E1.46.1.1", {"start": v(28.77, -2.4) * mm, "end": v(29.27, -2.4) * mm});
            skLineSegment(sketch, "E1.46.1.2", {"start": v(29.27, -4.6) * mm, "end": v(29.27, -2.4) * mm});
            skLineSegment(sketch, "E1.46.1.3", {"start": v(28.77, -4.6) * mm, "end": v(29.27, -4.6) * mm});
            skLineSegment(sketch, "E1.47.0.0", {"start": v(29.57, 0) * mm, "end": v(29.57, 2.2) * mm});
            skLineSegment(sketch, "E1.47.0.1", {"start": v(29.57, 2.2) * mm, "end": v(30.07, 2.2) * mm});
            skLineSegment(sketch, "E1.47.0.2", {"start": v(30.07, 0) * mm, "end": v(30.07, 2.2) * mm});
            skLineSegment(sketch, "E1.47.0.3", {"start": v(29.57, 0) * mm, "end": v(30.07, 0) * mm});
            skLineSegment(sketch, "E1.47.1.0", {"start": v(29.57, -4.6) * mm, "end": v(29.57, -2.4) * mm});
            skLineSegment(sketch, "E1.47.1.1", {"start": v(29.57, -2.4) * mm, "end": v(30.07, -2.4) * mm});
            skLineSegment(sketch, "E1.47.1.2", {"start": v(30.07, -4.6) * mm, "end": v(30.07, -2.4) * mm});
            skLineSegment(sketch, "E1.47.1.3", {"start": v(29.57, -4.6) * mm, "end": v(30.07, -4.6) * mm});
            skLineSegment(sketch, "E1.48.0.0", {"start": v(30.37, 0) * mm, "end": v(30.37, 2.2) * mm});
            skLineSegment(sketch, "E1.48.0.1", {"start": v(30.37, 2.2) * mm, "end": v(30.87, 2.2) * mm});
            skLineSegment(sketch, "E1.48.0.2", {"start": v(30.87, 0) * mm, "end": v(30.87, 2.2) * mm});
            skLineSegment(sketch, "E1.48.0.3", {"start": v(30.37, 0) * mm, "end": v(30.87, 0) * mm});
            skLineSegment(sketch, "E1.48.1.0", {"start": v(30.37, -4.6) * mm, "end": v(30.37, -2.4) * mm});
            skLineSegment(sketch, "E1.48.1.1", {"start": v(30.37, -2.4) * mm, "end": v(30.87, -2.4) * mm});
            skLineSegment(sketch, "E1.48.1.2", {"start": v(30.87, -4.6) * mm, "end": v(30.87, -2.4) * mm});
            skLineSegment(sketch, "E1.48.1.3", {"start": v(30.37, -4.6) * mm, "end": v(30.87, -4.6) * mm});
            skLineSegment(sketch, "E1.49.0.0", {"start": v(31.17, 0) * mm, "end": v(31.17, 2.2) * mm});
            skLineSegment(sketch, "E1.49.0.1", {"start": v(31.17, 2.2) * mm, "end": v(31.67, 2.2) * mm});
            skLineSegment(sketch, "E1.49.0.2", {"start": v(31.67, 0) * mm, "end": v(31.67, 2.2) * mm});
            skLineSegment(sketch, "E1.49.0.3", {"start": v(31.17, 0) * mm, "end": v(31.67, 0) * mm});
            skLineSegment(sketch, "E1.49.1.0", {"start": v(31.17, -4.6) * mm, "end": v(31.17, -2.4) * mm});
            skLineSegment(sketch, "E1.49.1.1", {"start": v(31.17, -2.4) * mm, "end": v(31.67, -2.4) * mm});
            skLineSegment(sketch, "E1.49.1.2", {"start": v(31.67, -4.6) * mm, "end": v(31.67, -2.4) * mm});
            skLineSegment(sketch, "E1.49.1.3", {"start": v(31.17, -4.6) * mm, "end": v(31.67, -4.6) * mm});
            skLineSegment(sketch, "E1.50.0.0", {"start": v(31.97, 0) * mm, "end": v(31.97, 2.2) * mm});
            skLineSegment(sketch, "E1.50.0.1", {"start": v(31.97, 2.2) * mm, "end": v(32.47, 2.2) * mm});
            skLineSegment(sketch, "E1.50.0.2", {"start": v(32.47, 0) * mm, "end": v(32.47, 2.2) * mm});
            skLineSegment(sketch, "E1.50.0.3", {"start": v(31.97, 0) * mm, "end": v(32.47, 0) * mm});
            skLineSegment(sketch, "E1.50.1.0", {"start": v(31.97, -4.6) * mm, "end": v(31.97, -2.4) * mm});
            skLineSegment(sketch, "E1.50.1.1", {"start": v(31.97, -2.4) * mm, "end": v(32.47, -2.4) * mm});
            skLineSegment(sketch, "E1.50.1.2", {"start": v(32.47, -4.6) * mm, "end": v(32.47, -2.4) * mm});
            skLineSegment(sketch, "E1.50.1.3", {"start": v(31.97, -4.6) * mm, "end": v(32.47, -4.6) * mm});
            skLineSegment(sketch, "E1.51.0.0", {"start": v(32.77, 0) * mm, "end": v(32.77, 2.2) * mm});
            skLineSegment(sketch, "E1.51.0.1", {"start": v(32.77, 2.2) * mm, "end": v(33.27, 2.2) * mm});
            skLineSegment(sketch, "E1.51.0.2", {"start": v(33.27, 0) * mm, "end": v(33.27, 2.2) * mm});
            skLineSegment(sketch, "E1.51.0.3", {"start": v(32.77, 0) * mm, "end": v(33.27, 0) * mm});
            skLineSegment(sketch, "E1.51.1.0", {"start": v(32.77, -4.6) * mm, "end": v(32.77, -2.4) * mm});
            skLineSegment(sketch, "E1.51.1.1", {"start": v(32.77, -2.4) * mm, "end": v(33.27, -2.4) * mm});
            skLineSegment(sketch, "E1.51.1.2", {"start": v(33.27, -4.6) * mm, "end": v(33.27, -2.4) * mm});
            skLineSegment(sketch, "E1.51.1.3", {"start": v(32.77, -4.6) * mm, "end": v(33.27, -4.6) * mm});
            skLineSegment(sketch, "E1.52.0.0", {"start": v(33.57, 0) * mm, "end": v(33.57, 2.2) * mm});
            skLineSegment(sketch, "E1.52.0.1", {"start": v(33.57, 2.2) * mm, "end": v(34.07, 2.2) * mm});
            skLineSegment(sketch, "E1.52.0.2", {"start": v(34.07, 0) * mm, "end": v(34.07, 2.2) * mm});
            skLineSegment(sketch, "E1.52.0.3", {"start": v(33.57, 0) * mm, "end": v(34.07, 0) * mm});
            skLineSegment(sketch, "E1.52.1.0", {"start": v(33.57, -4.6) * mm, "end": v(33.57, -2.4) * mm});
            skLineSegment(sketch, "E1.52.1.1", {"start": v(33.57, -2.4) * mm, "end": v(34.07, -2.4) * mm});
            skLineSegment(sketch, "E1.52.1.2", {"start": v(34.07, -4.6) * mm, "end": v(34.07, -2.4) * mm});
            skLineSegment(sketch, "E1.52.1.3", {"start": v(33.57, -4.6) * mm, "end": v(34.07, -4.6) * mm});
            skLineSegment(sketch, "E1.53.0.0", {"start": v(34.37, 0) * mm, "end": v(34.37, 2.2) * mm});
            skLineSegment(sketch, "E1.53.0.1", {"start": v(34.37, 2.2) * mm, "end": v(34.87, 2.2) * mm});
            skLineSegment(sketch, "E1.53.0.2", {"start": v(34.87, 0) * mm, "end": v(34.87, 2.2) * mm});
            skLineSegment(sketch, "E1.53.0.3", {"start": v(34.37, 0) * mm, "end": v(34.87, 0) * mm});
            skLineSegment(sketch, "E1.53.1.0", {"start": v(34.37, -4.6) * mm, "end": v(34.37, -2.4) * mm});
            skLineSegment(sketch, "E1.53.1.1", {"start": v(34.37, -2.4) * mm, "end": v(34.87, -2.4) * mm});
            skLineSegment(sketch, "E1.53.1.2", {"start": v(34.87, -4.6) * mm, "end": v(34.87, -2.4) * mm});
            skLineSegment(sketch, "E1.53.1.3", {"start": v(34.37, -4.6) * mm, "end": v(34.87, -4.6) * mm});
            skLineSegment(sketch, "E1.54.0.0", {"start": v(35.17, 0) * mm, "end": v(35.17, 2.2) * mm});
            skLineSegment(sketch, "E1.54.0.1", {"start": v(35.17, 2.2) * mm, "end": v(35.67, 2.2) * mm});
            skLineSegment(sketch, "E1.54.0.2", {"start": v(35.67, 0) * mm, "end": v(35.67, 2.2) * mm});
            skLineSegment(sketch, "E1.54.0.3", {"start": v(35.17, 0) * mm, "end": v(35.67, 0) * mm});
            skLineSegment(sketch, "E1.54.1.0", {"start": v(35.17, -4.6) * mm, "end": v(35.17, -2.4) * mm});
            skLineSegment(sketch, "E1.54.1.1", {"start": v(35.17, -2.4) * mm, "end": v(35.67, -2.4) * mm});
            skLineSegment(sketch, "E1.54.1.2", {"start": v(35.67, -4.6) * mm, "end": v(35.67, -2.4) * mm});
            skLineSegment(sketch, "E1.54.1.3", {"start": v(35.17, -4.6) * mm, "end": v(35.67, -4.6) * mm});
            skLineSegment(sketch, "E1.55.0.0", {"start": v(35.97, 0) * mm, "end": v(35.97, 2.2) * mm});
            skLineSegment(sketch, "E1.55.0.1", {"start": v(35.97, 2.2) * mm, "end": v(36.47, 2.2) * mm});
            skLineSegment(sketch, "E1.55.0.2", {"start": v(36.47, 0) * mm, "end": v(36.47, 2.2) * mm});
            skLineSegment(sketch, "E1.55.0.3", {"start": v(35.97, 0) * mm, "end": v(36.47, 0) * mm});
            skLineSegment(sketch, "E1.55.1.0", {"start": v(35.97, -4.6) * mm, "end": v(35.97, -2.4) * mm});
            skLineSegment(sketch, "E1.55.1.1", {"start": v(35.97, -2.4) * mm, "end": v(36.47, -2.4) * mm});
            skLineSegment(sketch, "E1.55.1.2", {"start": v(36.47, -4.6) * mm, "end": v(36.47, -2.4) * mm});
            skLineSegment(sketch, "E1.55.1.3", {"start": v(35.97, -4.6) * mm, "end": v(36.47, -4.6) * mm});
            skLineSegment(sketch, "E1.56.0.0", {"start": v(36.77, 0) * mm, "end": v(36.77, 2.2) * mm});
            skLineSegment(sketch, "E1.56.0.1", {"start": v(36.77, 2.2) * mm, "end": v(37.27, 2.2) * mm});
            skLineSegment(sketch, "E1.56.0.2", {"start": v(37.27, 0) * mm, "end": v(37.27, 2.2) * mm});
            skLineSegment(sketch, "E1.56.0.3", {"start": v(36.77, 0) * mm, "end": v(37.27, 0) * mm});
            skLineSegment(sketch, "E1.56.1.0", {"start": v(36.77, -4.6) * mm, "end": v(36.77, -2.4) * mm});
            skLineSegment(sketch, "E1.56.1.1", {"start": v(36.77, -2.4) * mm, "end": v(37.27, -2.4) * mm});
            skLineSegment(sketch, "E1.56.1.2", {"start": v(37.27, -4.6) * mm, "end": v(37.27, -2.4) * mm});
            skLineSegment(sketch, "E1.56.1.3", {"start": v(36.77, -4.6) * mm, "end": v(37.27, -4.6) * mm});
            skLineSegment(sketch, "E1.57.0.0", {"start": v(37.57, 0) * mm, "end": v(37.57, 2.2) * mm});
            skLineSegment(sketch, "E1.57.0.1", {"start": v(37.57, 2.2) * mm, "end": v(38.07, 2.2) * mm});
            skLineSegment(sketch, "E1.57.0.2", {"start": v(38.07, 0) * mm, "end": v(38.07, 2.2) * mm});
            skLineSegment(sketch, "E1.57.0.3", {"start": v(37.57, 0) * mm, "end": v(38.07, 0) * mm});
            skLineSegment(sketch, "E1.57.1.0", {"start": v(37.57, -4.6) * mm, "end": v(37.57, -2.4) * mm});
            skLineSegment(sketch, "E1.57.1.1", {"start": v(37.57, -2.4) * mm, "end": v(38.07, -2.4) * mm});
            skLineSegment(sketch, "E1.57.1.2", {"start": v(38.07, -4.6) * mm, "end": v(38.07, -2.4) * mm});
            skLineSegment(sketch, "E1.57.1.3", {"start": v(37.57, -4.6) * mm, "end": v(38.07, -4.6) * mm});
            skLineSegment(sketch, "E1.58.0.0", {"start": v(38.37, 0) * mm, "end": v(38.37, 2.2) * mm});
            skLineSegment(sketch, "E1.58.0.1", {"start": v(38.37, 2.2) * mm, "end": v(38.87, 2.2) * mm});
            skLineSegment(sketch, "E1.58.0.2", {"start": v(38.87, 0) * mm, "end": v(38.87, 2.2) * mm});
            skLineSegment(sketch, "E1.58.0.3", {"start": v(38.37, 0) * mm, "end": v(38.87, 0) * mm});
            skLineSegment(sketch, "E1.58.1.0", {"start": v(38.37, -4.6) * mm, "end": v(38.37, -2.4) * mm});
            skLineSegment(sketch, "E1.58.1.1", {"start": v(38.37, -2.4) * mm, "end": v(38.87, -2.4) * mm});
            skLineSegment(sketch, "E1.58.1.2", {"start": v(38.87, -4.6) * mm, "end": v(38.87, -2.4) * mm});
            skLineSegment(sketch, "E1.58.1.3", {"start": v(38.37, -4.6) * mm, "end": v(38.87, -4.6) * mm});
            skLineSegment(sketch, "E1.59.0.0", {"start": v(39.17, 0) * mm, "end": v(39.17, 2.2) * mm});
            skLineSegment(sketch, "E1.59.0.1", {"start": v(39.17, 2.2) * mm, "end": v(39.67, 2.2) * mm});
            skLineSegment(sketch, "E1.59.0.2", {"start": v(39.67, 0) * mm, "end": v(39.67, 2.2) * mm});
            skLineSegment(sketch, "E1.59.0.3", {"start": v(39.17, 0) * mm, "end": v(39.67, 0) * mm});
            skLineSegment(sketch, "E1.59.1.0", {"start": v(39.17, -4.6) * mm, "end": v(39.17, -2.4) * mm});
            skLineSegment(sketch, "E1.59.1.1", {"start": v(39.17, -2.4) * mm, "end": v(39.67, -2.4) * mm});
            skLineSegment(sketch, "E1.59.1.2", {"start": v(39.67, -4.6) * mm, "end": v(39.67, -2.4) * mm});
            skLineSegment(sketch, "E1.59.1.3", {"start": v(39.17, -4.6) * mm, "end": v(39.67, -4.6) * mm});
            skLineSegment(sketch, "E1.60.0.0", {"start": v(39.97, 0) * mm, "end": v(39.97, 2.2) * mm});
            skLineSegment(sketch, "E1.60.0.1", {"start": v(39.97, 2.2) * mm, "end": v(40.47, 2.2) * mm});
            skLineSegment(sketch, "E1.60.0.2", {"start": v(40.47, 0) * mm, "end": v(40.47, 2.2) * mm});
            skLineSegment(sketch, "E1.60.0.3", {"start": v(39.97, 0) * mm, "end": v(40.47, 0) * mm});
            skLineSegment(sketch, "E1.60.1.0", {"start": v(39.97, -4.6) * mm, "end": v(39.97, -2.4) * mm});
            skLineSegment(sketch, "E1.60.1.1", {"start": v(39.97, -2.4) * mm, "end": v(40.47, -2.4) * mm});
            skLineSegment(sketch, "E1.60.1.2", {"start": v(40.47, -4.6) * mm, "end": v(40.47, -2.4) * mm});
            skLineSegment(sketch, "E1.60.1.3", {"start": v(39.97, -4.6) * mm, "end": v(40.47, -4.6) * mm});
            skLineSegment(sketch, "E1.61.0.0", {"start": v(40.77, 0) * mm, "end": v(40.77, 2.2) * mm});
            skLineSegment(sketch, "E1.61.0.1", {"start": v(40.77, 2.2) * mm, "end": v(41.27, 2.2) * mm});
            skLineSegment(sketch, "E1.61.0.2", {"start": v(41.27, 0) * mm, "end": v(41.27, 2.2) * mm});
            skLineSegment(sketch, "E1.61.0.3", {"start": v(40.77, 0) * mm, "end": v(41.27, 0) * mm});
            skLineSegment(sketch, "E1.61.1.0", {"start": v(40.77, -4.6) * mm, "end": v(40.77, -2.4) * mm});
            skLineSegment(sketch, "E1.61.1.1", {"start": v(40.77, -2.4) * mm, "end": v(41.27, -2.4) * mm});
            skLineSegment(sketch, "E1.61.1.2", {"start": v(41.27, -4.6) * mm, "end": v(41.27, -2.4) * mm});
            skLineSegment(sketch, "E1.61.1.3", {"start": v(40.77, -4.6) * mm, "end": v(41.27, -4.6) * mm});
            skLineSegment(sketch, "E1.62.0.0", {"start": v(41.57, 0) * mm, "end": v(41.57, 2.2) * mm});
            skLineSegment(sketch, "E1.62.0.1", {"start": v(41.57, 2.2) * mm, "end": v(42.07, 2.2) * mm});
            skLineSegment(sketch, "E1.62.0.2", {"start": v(42.07, 0) * mm, "end": v(42.07, 2.2) * mm});
            skLineSegment(sketch, "E1.62.0.3", {"start": v(41.57, 0) * mm, "end": v(42.07, 0) * mm});
            skLineSegment(sketch, "E1.62.1.0", {"start": v(41.57, -4.6) * mm, "end": v(41.57, -2.4) * mm});
            skLineSegment(sketch, "E1.62.1.1", {"start": v(41.57, -2.4) * mm, "end": v(42.07, -2.4) * mm});
            skLineSegment(sketch, "E1.62.1.2", {"start": v(42.07, -4.6) * mm, "end": v(42.07, -2.4) * mm});
            skLineSegment(sketch, "E1.62.1.3", {"start": v(41.57, -4.6) * mm, "end": v(42.07, -4.6) * mm});
            skLineSegment(sketch, "E1.63.0.0", {"start": v(42.37, 0) * mm, "end": v(42.37, 2.2) * mm});
            skLineSegment(sketch, "E1.63.0.1", {"start": v(42.37, 2.2) * mm, "end": v(42.87, 2.2) * mm});
            skLineSegment(sketch, "E1.63.0.2", {"start": v(42.87, 0) * mm, "end": v(42.87, 2.2) * mm});
            skLineSegment(sketch, "E1.63.0.3", {"start": v(42.37, 0) * mm, "end": v(42.87, 0) * mm});
            skLineSegment(sketch, "E1.63.1.0", {"start": v(42.37, -4.6) * mm, "end": v(42.37, -2.4) * mm});
            skLineSegment(sketch, "E1.63.1.1", {"start": v(42.37, -2.4) * mm, "end": v(42.87, -2.4) * mm});
            skLineSegment(sketch, "E1.63.1.2", {"start": v(42.87, -4.6) * mm, "end": v(42.87, -2.4) * mm});
            skLineSegment(sketch, "E1.63.1.3", {"start": v(42.37, -4.6) * mm, "end": v(42.87, -4.6) * mm});
            skLineSegment(sketch, "E1.64.0.0", {"start": v(43.17, 0) * mm, "end": v(43.17, 2.2) * mm});
            skLineSegment(sketch, "E1.64.0.1", {"start": v(43.17, 2.2) * mm, "end": v(43.67, 2.2) * mm});
            skLineSegment(sketch, "E1.64.0.2", {"start": v(43.67, 0) * mm, "end": v(43.67, 2.2) * mm});
            skLineSegment(sketch, "E1.64.0.3", {"start": v(43.17, 0) * mm, "end": v(43.67, 0) * mm});
            skLineSegment(sketch, "E1.64.1.0", {"start": v(43.17, -4.6) * mm, "end": v(43.17, -2.4) * mm});
            skLineSegment(sketch, "E1.64.1.1", {"start": v(43.17, -2.4) * mm, "end": v(43.67, -2.4) * mm});
            skLineSegment(sketch, "E1.64.1.2", {"start": v(43.67, -4.6) * mm, "end": v(43.67, -2.4) * mm});
            skLineSegment(sketch, "E1.64.1.3", {"start": v(43.17, -4.6) * mm, "end": v(43.67, -4.6) * mm});
            skLineSegment(sketch, "E1.65.0.0", {"start": v(43.97, 0) * mm, "end": v(43.97, 2.2) * mm});
            skLineSegment(sketch, "E1.65.0.1", {"start": v(43.97, 2.2) * mm, "end": v(44.47, 2.2) * mm});
            skLineSegment(sketch, "E1.65.0.2", {"start": v(44.47, 0) * mm, "end": v(44.47, 2.2) * mm});
            skLineSegment(sketch, "E1.65.0.3", {"start": v(43.97, 0) * mm, "end": v(44.47, 0) * mm});
            skLineSegment(sketch, "E1.65.1.0", {"start": v(43.97, -4.6) * mm, "end": v(43.97, -2.4) * mm});
            skLineSegment(sketch, "E1.65.1.1", {"start": v(43.97, -2.4) * mm, "end": v(44.47, -2.4) * mm});
            skLineSegment(sketch, "E1.65.1.2", {"start": v(44.47, -4.6) * mm, "end": v(44.47, -2.4) * mm});
            skLineSegment(sketch, "E1.65.1.3", {"start": v(43.97, -4.6) * mm, "end": v(44.47, -4.6) * mm});
            skLineSegment(sketch, "E1.66.0.0", {"start": v(44.77, 0) * mm, "end": v(44.77, 2.2) * mm});
            skLineSegment(sketch, "E1.66.0.1", {"start": v(44.77, 2.2) * mm, "end": v(45.27, 2.2) * mm});
            skLineSegment(sketch, "E1.66.0.2", {"start": v(45.27, 0) * mm, "end": v(45.27, 2.2) * mm});
            skLineSegment(sketch, "E1.66.0.3", {"start": v(44.77, 0) * mm, "end": v(45.27, 0) * mm});
            skLineSegment(sketch, "E1.66.1.0", {"start": v(44.77, -4.6) * mm, "end": v(44.77, -2.4) * mm});
            skLineSegment(sketch, "E1.66.1.1", {"start": v(44.77, -2.4) * mm, "end": v(45.27, -2.4) * mm});
            skLineSegment(sketch, "E1.66.1.2", {"start": v(45.27, -4.6) * mm, "end": v(45.27, -2.4) * mm});
            skLineSegment(sketch, "E1.66.1.3", {"start": v(44.77, -4.6) * mm, "end": v(45.27, -4.6) * mm});
            skLineSegment(sketch, "E1.67.0.0", {"start": v(45.57, 0) * mm, "end": v(45.57, 2.2) * mm});
            skLineSegment(sketch, "E1.67.0.1", {"start": v(45.57, 2.2) * mm, "end": v(46.07, 2.2) * mm});
            skLineSegment(sketch, "E1.67.0.2", {"start": v(46.07, 0) * mm, "end": v(46.07, 2.2) * mm});
            skLineSegment(sketch, "E1.67.0.3", {"start": v(45.57, 0) * mm, "end": v(46.07, 0) * mm});
            skLineSegment(sketch, "E1.67.1.0", {"start": v(45.57, -4.6) * mm, "end": v(45.57, -2.4) * mm});
            skLineSegment(sketch, "E1.67.1.1", {"start": v(45.57, -2.4) * mm, "end": v(46.07, -2.4) * mm});
            skLineSegment(sketch, "E1.67.1.2", {"start": v(46.07, -4.6) * mm, "end": v(46.07, -2.4) * mm});
            skLineSegment(sketch, "E1.67.1.3", {"start": v(45.57, -4.6) * mm, "end": v(46.07, -4.6) * mm});
            skLineSegment(sketch, "E1.68.0.0", {"start": v(46.37, 0) * mm, "end": v(46.37, 2.2) * mm});
            skLineSegment(sketch, "E1.68.0.1", {"start": v(46.37, 2.2) * mm, "end": v(46.87, 2.2) * mm});
            skLineSegment(sketch, "E1.68.0.2", {"start": v(46.87, 0) * mm, "end": v(46.87, 2.2) * mm});
            skLineSegment(sketch, "E1.68.0.3", {"start": v(46.37, 0) * mm, "end": v(46.87, 0) * mm});
            skLineSegment(sketch, "E1.68.1.0", {"start": v(46.37, -4.6) * mm, "end": v(46.37, -2.4) * mm});
            skLineSegment(sketch, "E1.68.1.1", {"start": v(46.37, -2.4) * mm, "end": v(46.87, -2.4) * mm});
            skLineSegment(sketch, "E1.68.1.2", {"start": v(46.87, -4.6) * mm, "end": v(46.87, -2.4) * mm});
            skLineSegment(sketch, "E1.68.1.3", {"start": v(46.37, -4.6) * mm, "end": v(46.87, -4.6) * mm});
            skLineSegment(sketch, "E1.69.0.0", {"start": v(47.17, 0) * mm, "end": v(47.17, 2.2) * mm});
            skLineSegment(sketch, "E1.69.0.1", {"start": v(47.17, 2.2) * mm, "end": v(47.67, 2.2) * mm});
            skLineSegment(sketch, "E1.69.0.2", {"start": v(47.67, 0) * mm, "end": v(47.67, 2.2) * mm});
            skLineSegment(sketch, "E1.69.0.3", {"start": v(47.17, 0) * mm, "end": v(47.67, 0) * mm});
            skLineSegment(sketch, "E1.69.1.0", {"start": v(47.17, -4.6) * mm, "end": v(47.17, -2.4) * mm});
            skLineSegment(sketch, "E1.69.1.1", {"start": v(47.17, -2.4) * mm, "end": v(47.67, -2.4) * mm});
            skLineSegment(sketch, "E1.69.1.2", {"start": v(47.67, -4.6) * mm, "end": v(47.67, -2.4) * mm});
            skLineSegment(sketch, "E1.69.1.3", {"start": v(47.17, -4.6) * mm, "end": v(47.67, -4.6) * mm});
            skLineSegment(sketch, "E1.70.0.0", {"start": v(47.97, 0) * mm, "end": v(47.97, 2.2) * mm});
            skLineSegment(sketch, "E1.70.0.1", {"start": v(47.97, 2.2) * mm, "end": v(48.47, 2.2) * mm});
            skLineSegment(sketch, "E1.70.0.2", {"start": v(48.47, 0) * mm, "end": v(48.47, 2.2) * mm});
            skLineSegment(sketch, "E1.70.0.3", {"start": v(47.97, 0) * mm, "end": v(48.47, 0) * mm});
            skLineSegment(sketch, "E1.70.1.0", {"start": v(47.97, -4.6) * mm, "end": v(47.97, -2.4) * mm});
            skLineSegment(sketch, "E1.70.1.1", {"start": v(47.97, -2.4) * mm, "end": v(48.47, -2.4) * mm});
            skLineSegment(sketch, "E1.70.1.2", {"start": v(48.47, -4.6) * mm, "end": v(48.47, -2.4) * mm});
            skLineSegment(sketch, "E1.70.1.3", {"start": v(47.97, -4.6) * mm, "end": v(48.47, -4.6) * mm});
            skLineSegment(sketch, "E1.71.0.0", {"start": v(48.77, 0) * mm, "end": v(48.77, 2.2) * mm});
            skLineSegment(sketch, "E1.71.0.1", {"start": v(48.77, 2.2) * mm, "end": v(49.27, 2.2) * mm});
            skLineSegment(sketch, "E1.71.0.2", {"start": v(49.27, 0) * mm, "end": v(49.27, 2.2) * mm});
            skLineSegment(sketch, "E1.71.0.3", {"start": v(48.77, 0) * mm, "end": v(49.27, 0) * mm});
            skLineSegment(sketch, "E1.71.1.0", {"start": v(48.77, -4.6) * mm, "end": v(48.77, -2.4) * mm});
            skLineSegment(sketch, "E1.71.1.1", {"start": v(48.77, -2.4) * mm, "end": v(49.27, -2.4) * mm});
            skLineSegment(sketch, "E1.71.1.2", {"start": v(49.27, -4.6) * mm, "end": v(49.27, -2.4) * mm});
            skLineSegment(sketch, "E1.71.1.3", {"start": v(48.77, -4.6) * mm, "end": v(49.27, -4.6) * mm});
            skLineSegment(sketch, "E1.72.0.0", {"start": v(49.57, 0) * mm, "end": v(49.57, 2.2) * mm});
            skLineSegment(sketch, "E1.72.0.1", {"start": v(49.57, 2.2) * mm, "end": v(50.07, 2.2) * mm});
            skLineSegment(sketch, "E1.72.0.2", {"start": v(50.07, 0) * mm, "end": v(50.07, 2.2) * mm});
            skLineSegment(sketch, "E1.72.0.3", {"start": v(49.57, 0) * mm, "end": v(50.07, 0) * mm});
            skLineSegment(sketch, "E1.72.1.0", {"start": v(49.57, -4.6) * mm, "end": v(49.57, -2.4) * mm});
            skLineSegment(sketch, "E1.72.1.1", {"start": v(49.57, -2.4) * mm, "end": v(50.07, -2.4) * mm});
            skLineSegment(sketch, "E1.72.1.2", {"start": v(50.07, -4.6) * mm, "end": v(50.07, -2.4) * mm});
            skLineSegment(sketch, "E1.72.1.3", {"start": v(49.57, -4.6) * mm, "end": v(50.07, -4.6) * mm});
            skLineSegment(sketch, "E1.73.0.0", {"start": v(50.37, 0) * mm, "end": v(50.37, 2.2) * mm});
            skLineSegment(sketch, "E1.73.0.1", {"start": v(50.37, 2.2) * mm, "end": v(50.87, 2.2) * mm});
            skLineSegment(sketch, "E1.73.0.2", {"start": v(50.87, 0) * mm, "end": v(50.87, 2.2) * mm});
            skLineSegment(sketch, "E1.73.0.3", {"start": v(50.37, 0) * mm, "end": v(50.87, 0) * mm});
            skLineSegment(sketch, "E1.73.1.0", {"start": v(50.37, -4.6) * mm, "end": v(50.37, -2.4) * mm});
            skLineSegment(sketch, "E1.73.1.1", {"start": v(50.37, -2.4) * mm, "end": v(50.87, -2.4) * mm});
            skLineSegment(sketch, "E1.73.1.2", {"start": v(50.87, -4.6) * mm, "end": v(50.87, -2.4) * mm});
            skLineSegment(sketch, "E1.73.1.3", {"start": v(50.37, -4.6) * mm, "end": v(50.87, -4.6) * mm});
            skLineSegment(sketch, "E1.74.0.0", {"start": v(51.17, 0) * mm, "end": v(51.17, 2.2) * mm});
            skLineSegment(sketch, "E1.74.0.1", {"start": v(51.17, 2.2) * mm, "end": v(51.67, 2.2) * mm});
            skLineSegment(sketch, "E1.74.0.2", {"start": v(51.67, 0) * mm, "end": v(51.67, 2.2) * mm});
            skLineSegment(sketch, "E1.74.0.3", {"start": v(51.17, 0) * mm, "end": v(51.67, 0) * mm});
            skLineSegment(sketch, "E1.74.1.0", {"start": v(51.17, -4.6) * mm, "end": v(51.17, -2.4) * mm});
            skLineSegment(sketch, "E1.74.1.1", {"start": v(51.17, -2.4) * mm, "end": v(51.67, -2.4) * mm});
            skLineSegment(sketch, "E1.74.1.2", {"start": v(51.67, -4.6) * mm, "end": v(51.67, -2.4) * mm});
            skLineSegment(sketch, "E1.74.1.3", {"start": v(51.17, -4.6) * mm, "end": v(51.67, -4.6) * mm});
            skLineSegment(sketch, "E1.75.0.0", {"start": v(51.97, 0) * mm, "end": v(51.97, 2.2) * mm});
            skLineSegment(sketch, "E1.75.0.1", {"start": v(51.97, 2.2) * mm, "end": v(52.47, 2.2) * mm});
            skLineSegment(sketch, "E1.75.0.2", {"start": v(52.47, 0) * mm, "end": v(52.47, 2.2) * mm});
            skLineSegment(sketch, "E1.75.0.3", {"start": v(51.97, 0) * mm, "end": v(52.47, 0) * mm});
            skLineSegment(sketch, "E1.75.1.0", {"start": v(51.97, -4.6) * mm, "end": v(51.97, -2.4) * mm});
            skLineSegment(sketch, "E1.75.1.1", {"start": v(51.97, -2.4) * mm, "end": v(52.47, -2.4) * mm});
            skLineSegment(sketch, "E1.75.1.2", {"start": v(52.47, -4.6) * mm, "end": v(52.47, -2.4) * mm});
            skLineSegment(sketch, "E1.75.1.3", {"start": v(51.97, -4.6) * mm, "end": v(52.47, -4.6) * mm});
            skLineSegment(sketch, "E1.76.0.0", {"start": v(52.77, 0) * mm, "end": v(52.77, 2.2) * mm});
            skLineSegment(sketch, "E1.76.0.1", {"start": v(52.77, 2.2) * mm, "end": v(53.27, 2.2) * mm});
            skLineSegment(sketch, "E1.76.0.2", {"start": v(53.27, 0) * mm, "end": v(53.27, 2.2) * mm});
            skLineSegment(sketch, "E1.76.0.3", {"start": v(52.77, 0) * mm, "end": v(53.27, 0) * mm});
            skLineSegment(sketch, "E1.76.1.0", {"start": v(52.77, -4.6) * mm, "end": v(52.77, -2.4) * mm});
            skLineSegment(sketch, "E1.76.1.1", {"start": v(52.77, -2.4) * mm, "end": v(53.27, -2.4) * mm});
            skLineSegment(sketch, "E1.76.1.2", {"start": v(53.27, -4.6) * mm, "end": v(53.27, -2.4) * mm});
            skLineSegment(sketch, "E1.76.1.3", {"start": v(52.77, -4.6) * mm, "end": v(53.27, -4.6) * mm});
            skLineSegment(sketch, "E1.77.0.0", {"start": v(53.57, 0) * mm, "end": v(53.57, 2.2) * mm});
            skLineSegment(sketch, "E1.77.0.1", {"start": v(53.57, 2.2) * mm, "end": v(54.07, 2.2) * mm});
            skLineSegment(sketch, "E1.77.0.2", {"start": v(54.07, 0) * mm, "end": v(54.07, 2.2) * mm});
            skLineSegment(sketch, "E1.77.0.3", {"start": v(53.57, 0) * mm, "end": v(54.07, 0) * mm});
            skLineSegment(sketch, "E1.77.1.0", {"start": v(53.57, -4.6) * mm, "end": v(53.57, -2.4) * mm});
            skLineSegment(sketch, "E1.77.1.1", {"start": v(53.57, -2.4) * mm, "end": v(54.07, -2.4) * mm});
            skLineSegment(sketch, "E1.77.1.2", {"start": v(54.07, -4.6) * mm, "end": v(54.07, -2.4) * mm});
            skLineSegment(sketch, "E1.77.1.3", {"start": v(53.57, -4.6) * mm, "end": v(54.07, -4.6) * mm});
            skLineSegment(sketch, "E1.78.0.0", {"start": v(54.37, 0) * mm, "end": v(54.37, 2.2) * mm});
            skLineSegment(sketch, "E1.78.0.1", {"start": v(54.37, 2.2) * mm, "end": v(54.87, 2.2) * mm});
            skLineSegment(sketch, "E1.78.0.2", {"start": v(54.87, 0) * mm, "end": v(54.87, 2.2) * mm});
            skLineSegment(sketch, "E1.78.0.3", {"start": v(54.37, 0) * mm, "end": v(54.87, 0) * mm});
            skLineSegment(sketch, "E1.78.1.0", {"start": v(54.37, -4.6) * mm, "end": v(54.37, -2.4) * mm});
            skLineSegment(sketch, "E1.78.1.1", {"start": v(54.37, -2.4) * mm, "end": v(54.87, -2.4) * mm});
            skLineSegment(sketch, "E1.78.1.2", {"start": v(54.87, -4.6) * mm, "end": v(54.87, -2.4) * mm});
            skLineSegment(sketch, "E1.78.1.3", {"start": v(54.37, -4.6) * mm, "end": v(54.87, -4.6) * mm});
            skLineSegment(sketch, "E1.79.0.0", {"start": v(55.17, 0) * mm, "end": v(55.17, 2.2) * mm});
            skLineSegment(sketch, "E1.79.0.1", {"start": v(55.17, 2.2) * mm, "end": v(55.67, 2.2) * mm});
            skLineSegment(sketch, "E1.79.0.2", {"start": v(55.67, 0) * mm, "end": v(55.67, 2.2) * mm});
            skLineSegment(sketch, "E1.79.0.3", {"start": v(55.17, 0) * mm, "end": v(55.67, 0) * mm});
            skLineSegment(sketch, "E1.79.1.0", {"start": v(55.17, -4.6) * mm, "end": v(55.17, -2.4) * mm});
            skLineSegment(sketch, "E1.79.1.1", {"start": v(55.17, -2.4) * mm, "end": v(55.67, -2.4) * mm});
            skLineSegment(sketch, "E1.79.1.2", {"start": v(55.67, -4.6) * mm, "end": v(55.67, -2.4) * mm});
            skLineSegment(sketch, "E1.79.1.3", {"start": v(55.17, -4.6) * mm, "end": v(55.67, -4.6) * mm});
            skLineSegment(sketch, "E1.80.0.0", {"start": v(55.97, 0) * mm, "end": v(55.97, 2.2) * mm});
            skLineSegment(sketch, "E1.80.0.1", {"start": v(55.97, 2.2) * mm, "end": v(56.47, 2.2) * mm});
            skLineSegment(sketch, "E1.80.0.2", {"start": v(56.47, 0) * mm, "end": v(56.47, 2.2) * mm});
            skLineSegment(sketch, "E1.80.0.3", {"start": v(55.97, 0) * mm, "end": v(56.47, 0) * mm});
            skLineSegment(sketch, "E1.80.1.0", {"start": v(55.97, -4.6) * mm, "end": v(55.97, -2.4) * mm});
            skLineSegment(sketch, "E1.80.1.1", {"start": v(55.97, -2.4) * mm, "end": v(56.47, -2.4) * mm});
            skLineSegment(sketch, "E1.80.1.2", {"start": v(56.47, -4.6) * mm, "end": v(56.47, -2.4) * mm});
            skLineSegment(sketch, "E1.80.1.3", {"start": v(55.97, -4.6) * mm, "end": v(56.47, -4.6) * mm});
            skLineSegment(sketch, "E1.81.0.0", {"start": v(56.77, 0) * mm, "end": v(56.77, 2.2) * mm});
            skLineSegment(sketch, "E1.81.0.1", {"start": v(56.77, 2.2) * mm, "end": v(57.27, 2.2) * mm});
            skLineSegment(sketch, "E1.81.0.2", {"start": v(57.27, 0) * mm, "end": v(57.27, 2.2) * mm});
            skLineSegment(sketch, "E1.81.0.3", {"start": v(56.77, 0) * mm, "end": v(57.27, 0) * mm});
            skLineSegment(sketch, "E1.81.1.0", {"start": v(56.77, -4.6) * mm, "end": v(56.77, -2.4) * mm});
            skLineSegment(sketch, "E1.81.1.1", {"start": v(56.77, -2.4) * mm, "end": v(57.27, -2.4) * mm});
            skLineSegment(sketch, "E1.81.1.2", {"start": v(57.27, -4.6) * mm, "end": v(57.27, -2.4) * mm});
            skLineSegment(sketch, "E1.81.1.3", {"start": v(56.77, -4.6) * mm, "end": v(57.27, -4.6) * mm});
            skLineSegment(sketch, "E1.82.0.0", {"start": v(57.57, 0) * mm, "end": v(57.57, 2.2) * mm});
            skLineSegment(sketch, "E1.82.0.1", {"start": v(57.57, 2.2) * mm, "end": v(58.07, 2.2) * mm});
            skLineSegment(sketch, "E1.82.0.2", {"start": v(58.07, 0) * mm, "end": v(58.07, 2.2) * mm});
            skLineSegment(sketch, "E1.82.0.3", {"start": v(57.57, 0) * mm, "end": v(58.07, 0) * mm});
            skLineSegment(sketch, "E1.82.1.0", {"start": v(57.57, -4.6) * mm, "end": v(57.57, -2.4) * mm});
            skLineSegment(sketch, "E1.82.1.1", {"start": v(57.57, -2.4) * mm, "end": v(58.07, -2.4) * mm});
            skLineSegment(sketch, "E1.82.1.2", {"start": v(58.07, -4.6) * mm, "end": v(58.07, -2.4) * mm});
            skLineSegment(sketch, "E1.82.1.3", {"start": v(57.57, -4.6) * mm, "end": v(58.07, -4.6) * mm});
            skLineSegment(sketch, "E1.83.0.0", {"start": v(58.37, 0) * mm, "end": v(58.37, 2.2) * mm});
            skLineSegment(sketch, "E1.83.0.1", {"start": v(58.37, 2.2) * mm, "end": v(58.87, 2.2) * mm});
            skLineSegment(sketch, "E1.83.0.2", {"start": v(58.87, 0) * mm, "end": v(58.87, 2.2) * mm});
            skLineSegment(sketch, "E1.83.0.3", {"start": v(58.37, 0) * mm, "end": v(58.87, 0) * mm});
            skLineSegment(sketch, "E1.83.1.0", {"start": v(58.37, -4.6) * mm, "end": v(58.37, -2.4) * mm});
            skLineSegment(sketch, "E1.83.1.1", {"start": v(58.37, -2.4) * mm, "end": v(58.87, -2.4) * mm});
            skLineSegment(sketch, "E1.83.1.2", {"start": v(58.87, -4.6) * mm, "end": v(58.87, -2.4) * mm});
            skLineSegment(sketch, "E1.83.1.3", {"start": v(58.37, -4.6) * mm, "end": v(58.87, -4.6) * mm});
            skLineSegment(sketch, "E1.84.0.0", {"start": v(59.17, 0) * mm, "end": v(59.17, 2.2) * mm});
            skLineSegment(sketch, "E1.84.0.1", {"start": v(59.17, 2.2) * mm, "end": v(59.67, 2.2) * mm});
            skLineSegment(sketch, "E1.84.0.2", {"start": v(59.67, 0) * mm, "end": v(59.67, 2.2) * mm});
            skLineSegment(sketch, "E1.84.0.3", {"start": v(59.17, 0) * mm, "end": v(59.67, 0) * mm});
            skLineSegment(sketch, "E1.84.1.0", {"start": v(59.17, -4.6) * mm, "end": v(59.17, -2.4) * mm});
            skLineSegment(sketch, "E1.84.1.1", {"start": v(59.17, -2.4) * mm, "end": v(59.67, -2.4) * mm});
            skLineSegment(sketch, "E1.84.1.2", {"start": v(59.67, -4.6) * mm, "end": v(59.67, -2.4) * mm});
            skLineSegment(sketch, "E1.84.1.3", {"start": v(59.17, -4.6) * mm, "end": v(59.67, -4.6) * mm});
            skLineSegment(sketch, "E1.85.0.0", {"start": v(59.97, 0) * mm, "end": v(59.97, 2.2) * mm});
            skLineSegment(sketch, "E1.85.0.1", {"start": v(59.97, 2.2) * mm, "end": v(60.47, 2.2) * mm});
            skLineSegment(sketch, "E1.85.0.2", {"start": v(60.47, 0) * mm, "end": v(60.47, 2.2) * mm});
            skLineSegment(sketch, "E1.85.0.3", {"start": v(59.97, 0) * mm, "end": v(60.47, 0) * mm});
            skLineSegment(sketch, "E1.85.1.0", {"start": v(59.97, -4.6) * mm, "end": v(59.97, -2.4) * mm});
            skLineSegment(sketch, "E1.85.1.1", {"start": v(59.97, -2.4) * mm, "end": v(60.47, -2.4) * mm});
            skLineSegment(sketch, "E1.85.1.2", {"start": v(60.47, -4.6) * mm, "end": v(60.47, -2.4) * mm});
            skLineSegment(sketch, "E1.85.1.3", {"start": v(59.97, -4.6) * mm, "end": v(60.47, -4.6) * mm});
            skLineSegment(sketch, "E1.86.0.0", {"start": v(60.77, 0) * mm, "end": v(60.77, 2.2) * mm});
            skLineSegment(sketch, "E1.86.0.1", {"start": v(60.77, 2.2) * mm, "end": v(61.27, 2.2) * mm});
            skLineSegment(sketch, "E1.86.0.2", {"start": v(61.27, 0) * mm, "end": v(61.27, 2.2) * mm});
            skLineSegment(sketch, "E1.86.0.3", {"start": v(60.77, 0) * mm, "end": v(61.27, 0) * mm});
            skLineSegment(sketch, "E1.86.1.0", {"start": v(60.77, -4.6) * mm, "end": v(60.77, -2.4) * mm});
            skLineSegment(sketch, "E1.86.1.1", {"start": v(60.77, -2.4) * mm, "end": v(61.27, -2.4) * mm});
            skLineSegment(sketch, "E1.86.1.2", {"start": v(61.27, -4.6) * mm, "end": v(61.27, -2.4) * mm});
            skLineSegment(sketch, "E1.86.1.3", {"start": v(60.77, -4.6) * mm, "end": v(61.27, -4.6) * mm});
            skLineSegment(sketch, "E1.87.0.0", {"start": v(61.57, 0) * mm, "end": v(61.57, 2.2) * mm});
            skLineSegment(sketch, "E1.87.0.1", {"start": v(61.57, 2.2) * mm, "end": v(62.07, 2.2) * mm});
            skLineSegment(sketch, "E1.87.0.2", {"start": v(62.07, 0) * mm, "end": v(62.07, 2.2) * mm});
            skLineSegment(sketch, "E1.87.0.3", {"start": v(61.57, 0) * mm, "end": v(62.07, 0) * mm});
            skLineSegment(sketch, "E1.87.1.0", {"start": v(61.57, -4.6) * mm, "end": v(61.57, -2.4) * mm});
            skLineSegment(sketch, "E1.87.1.1", {"start": v(61.57, -2.4) * mm, "end": v(62.07, -2.4) * mm});
            skLineSegment(sketch, "E1.87.1.2", {"start": v(62.07, -4.6) * mm, "end": v(62.07, -2.4) * mm});
            skLineSegment(sketch, "E1.87.1.3", {"start": v(61.57, -4.6) * mm, "end": v(62.07, -4.6) * mm});
            skLineSegment(sketch, "E1.88.0.0", {"start": v(62.37, 0) * mm, "end": v(62.37, 2.2) * mm});
            skLineSegment(sketch, "E1.88.0.1", {"start": v(62.37, 2.2) * mm, "end": v(62.87, 2.2) * mm});
            skLineSegment(sketch, "E1.88.0.2", {"start": v(62.87, 0) * mm, "end": v(62.87, 2.2) * mm});
            skLineSegment(sketch, "E1.88.0.3", {"start": v(62.37, 0) * mm, "end": v(62.87, 0) * mm});
            skLineSegment(sketch, "E1.88.1.0", {"start": v(62.37, -4.6) * mm, "end": v(62.37, -2.4) * mm});
            skLineSegment(sketch, "E1.88.1.1", {"start": v(62.37, -2.4) * mm, "end": v(62.87, -2.4) * mm});
            skLineSegment(sketch, "E1.88.1.2", {"start": v(62.87, -4.6) * mm, "end": v(62.87, -2.4) * mm});
            skLineSegment(sketch, "E1.88.1.3", {"start": v(62.37, -4.6) * mm, "end": v(62.87, -4.6) * mm});
            skLineSegment(sketch, "E1.89.0.0", {"start": v(63.17, 0) * mm, "end": v(63.17, 2.2) * mm});
            skLineSegment(sketch, "E1.89.0.1", {"start": v(63.17, 2.2) * mm, "end": v(63.67, 2.2) * mm});
            skLineSegment(sketch, "E1.89.0.2", {"start": v(63.67, 0) * mm, "end": v(63.67, 2.2) * mm});
            skLineSegment(sketch, "E1.89.0.3", {"start": v(63.17, 0) * mm, "end": v(63.67, 0) * mm});
            skLineSegment(sketch, "E1.89.1.0", {"start": v(63.17, -4.6) * mm, "end": v(63.17, -2.4) * mm});
            skLineSegment(sketch, "E1.89.1.1", {"start": v(63.17, -2.4) * mm, "end": v(63.67, -2.4) * mm});
            skLineSegment(sketch, "E1.89.1.2", {"start": v(63.67, -4.6) * mm, "end": v(63.67, -2.4) * mm});
            skLineSegment(sketch, "E1.89.1.3", {"start": v(63.17, -4.6) * mm, "end": v(63.67, -4.6) * mm});
            skLineSegment(sketch, "E1.90.0.0", {"start": v(63.97, 0) * mm, "end": v(63.97, 2.2) * mm});
            skLineSegment(sketch, "E1.90.0.1", {"start": v(63.97, 2.2) * mm, "end": v(64.47, 2.2) * mm});
            skLineSegment(sketch, "E1.90.0.2", {"start": v(64.47, 0) * mm, "end": v(64.47, 2.2) * mm});
            skLineSegment(sketch, "E1.90.0.3", {"start": v(63.97, 0) * mm, "end": v(64.47, 0) * mm});
            skLineSegment(sketch, "E1.90.1.0", {"start": v(63.97, -4.6) * mm, "end": v(63.97, -2.4) * mm});
            skLineSegment(sketch, "E1.90.1.1", {"start": v(63.97, -2.4) * mm, "end": v(64.47, -2.4) * mm});
            skLineSegment(sketch, "E1.90.1.2", {"start": v(64.47, -4.6) * mm, "end": v(64.47, -2.4) * mm});
            skLineSegment(sketch, "E1.90.1.3", {"start": v(63.97, -4.6) * mm, "end": v(64.47, -4.6) * mm});
            skLineSegment(sketch, "E1.91.0.0", {"start": v(64.77, 0) * mm, "end": v(64.77, 2.2) * mm});
            skLineSegment(sketch, "E1.91.0.1", {"start": v(64.77, 2.2) * mm, "end": v(65.27, 2.2) * mm});
            skLineSegment(sketch, "E1.91.0.2", {"start": v(65.27, 0) * mm, "end": v(65.27, 2.2) * mm});
            skLineSegment(sketch, "E1.91.0.3", {"start": v(64.77, 0) * mm, "end": v(65.27, 0) * mm});
            skLineSegment(sketch, "E1.91.1.0", {"start": v(64.77, -4.6) * mm, "end": v(64.77, -2.4) * mm});
            skLineSegment(sketch, "E1.91.1.1", {"start": v(64.77, -2.4) * mm, "end": v(65.27, -2.4) * mm});
            skLineSegment(sketch, "E1.91.1.2", {"start": v(65.27, -4.6) * mm, "end": v(65.27, -2.4) * mm});
            skLineSegment(sketch, "E1.91.1.3", {"start": v(64.77, -4.6) * mm, "end": v(65.27, -4.6) * mm});
            skLineSegment(sketch, "E1.92.0.0", {"start": v(65.57, 0) * mm, "end": v(65.57, 2.2) * mm});
            skLineSegment(sketch, "E1.92.0.1", {"start": v(65.57, 2.2) * mm, "end": v(66.07, 2.2) * mm});
            skLineSegment(sketch, "E1.92.0.2", {"start": v(66.07, 0) * mm, "end": v(66.07, 2.2) * mm});
            skLineSegment(sketch, "E1.92.0.3", {"start": v(65.57, 0) * mm, "end": v(66.07, 0) * mm});
            skLineSegment(sketch, "E1.92.1.0", {"start": v(65.57, -4.6) * mm, "end": v(65.57, -2.4) * mm});
            skLineSegment(sketch, "E1.92.1.1", {"start": v(65.57, -2.4) * mm, "end": v(66.07, -2.4) * mm});
            skLineSegment(sketch, "E1.92.1.2", {"start": v(66.07, -4.6) * mm, "end": v(66.07, -2.4) * mm});
            skLineSegment(sketch, "E1.92.1.3", {"start": v(65.57, -4.6) * mm, "end": v(66.07, -4.6) * mm});
            skLineSegment(sketch, "E1.93.0.0", {"start": v(66.37, 0) * mm, "end": v(66.37, 2.2) * mm});
            skLineSegment(sketch, "E1.93.0.1", {"start": v(66.37, 2.2) * mm, "end": v(66.87, 2.2) * mm});
            skLineSegment(sketch, "E1.93.0.2", {"start": v(66.87, 0) * mm, "end": v(66.87, 2.2) * mm});
            skLineSegment(sketch, "E1.93.0.3", {"start": v(66.37, 0) * mm, "end": v(66.87, 0) * mm});
            skLineSegment(sketch, "E1.93.1.0", {"start": v(66.37, -4.6) * mm, "end": v(66.37, -2.4) * mm});
            skLineSegment(sketch, "E1.93.1.1", {"start": v(66.37, -2.4) * mm, "end": v(66.87, -2.4) * mm});
            skLineSegment(sketch, "E1.93.1.2", {"start": v(66.87, -4.6) * mm, "end": v(66.87, -2.4) * mm});
            skLineSegment(sketch, "E1.93.1.3", {"start": v(66.37, -4.6) * mm, "end": v(66.87, -4.6) * mm});
            skLineSegment(sketch, "E1.94.0.0", {"start": v(67.17, 0) * mm, "end": v(67.17, 2.2) * mm});
            skLineSegment(sketch, "E1.94.0.1", {"start": v(67.17, 2.2) * mm, "end": v(67.67, 2.2) * mm});
            skLineSegment(sketch, "E1.94.0.2", {"start": v(67.67, 0) * mm, "end": v(67.67, 2.2) * mm});
            skLineSegment(sketch, "E1.94.0.3", {"start": v(67.17, 0) * mm, "end": v(67.67, 0) * mm});
            skLineSegment(sketch, "E1.94.1.0", {"start": v(67.17, -4.6) * mm, "end": v(67.17, -2.4) * mm});
            skLineSegment(sketch, "E1.94.1.1", {"start": v(67.17, -2.4) * mm, "end": v(67.67, -2.4) * mm});
            skLineSegment(sketch, "E1.94.1.2", {"start": v(67.67, -4.6) * mm, "end": v(67.67, -2.4) * mm});
            skLineSegment(sketch, "E1.94.1.3", {"start": v(67.17, -4.6) * mm, "end": v(67.67, -4.6) * mm});
            skLineSegment(sketch, "E1.95.0.0", {"start": v(67.97, 0) * mm, "end": v(67.97, 2.2) * mm});
            skLineSegment(sketch, "E1.95.0.1", {"start": v(67.97, 2.2) * mm, "end": v(68.47, 2.2) * mm});
            skLineSegment(sketch, "E1.95.0.2", {"start": v(68.47, 0) * mm, "end": v(68.47, 2.2) * mm});
            skLineSegment(sketch, "E1.95.0.3", {"start": v(67.97, 0) * mm, "end": v(68.47, 0) * mm});
            skLineSegment(sketch, "E1.95.1.0", {"start": v(67.97, -4.6) * mm, "end": v(67.97, -2.4) * mm});
            skLineSegment(sketch, "E1.95.1.1", {"start": v(67.97, -2.4) * mm, "end": v(68.47, -2.4) * mm});
            skLineSegment(sketch, "E1.95.1.2", {"start": v(68.47, -4.6) * mm, "end": v(68.47, -2.4) * mm});
            skLineSegment(sketch, "E1.95.1.3", {"start": v(67.97, -4.6) * mm, "end": v(68.47, -4.6) * mm});
            skLineSegment(sketch, "E1.96.0.0", {"start": v(68.77, 0) * mm, "end": v(68.77, 2.2) * mm});
            skLineSegment(sketch, "E1.96.0.1", {"start": v(68.77, 2.2) * mm, "end": v(69.27, 2.2) * mm});
            skLineSegment(sketch, "E1.96.0.2", {"start": v(69.27, 0) * mm, "end": v(69.27, 2.2) * mm});
            skLineSegment(sketch, "E1.96.0.3", {"start": v(68.77, 0) * mm, "end": v(69.27, 0) * mm});
            skLineSegment(sketch, "E1.96.1.0", {"start": v(68.77, -4.6) * mm, "end": v(68.77, -2.4) * mm});
            skLineSegment(sketch, "E1.96.1.1", {"start": v(68.77, -2.4) * mm, "end": v(69.27, -2.4) * mm});
            skLineSegment(sketch, "E1.96.1.2", {"start": v(69.27, -4.6) * mm, "end": v(69.27, -2.4) * mm});
            skLineSegment(sketch, "E1.96.1.3", {"start": v(68.77, -4.6) * mm, "end": v(69.27, -4.6) * mm});
            skLineSegment(sketch, "E1.97.0.0", {"start": v(69.57, 0) * mm, "end": v(69.57, 2.2) * mm});
            skLineSegment(sketch, "E1.97.0.1", {"start": v(69.57, 2.2) * mm, "end": v(70.07, 2.2) * mm});
            skLineSegment(sketch, "E1.97.0.2", {"start": v(70.07, 0) * mm, "end": v(70.07, 2.2) * mm});
            skLineSegment(sketch, "E1.97.0.3", {"start": v(69.57, 0) * mm, "end": v(70.07, 0) * mm});
            skLineSegment(sketch, "E1.97.1.0", {"start": v(69.57, -4.6) * mm, "end": v(69.57, -2.4) * mm});
            skLineSegment(sketch, "E1.97.1.1", {"start": v(69.57, -2.4) * mm, "end": v(70.07, -2.4) * mm});
            skLineSegment(sketch, "E1.97.1.2", {"start": v(70.07, -4.6) * mm, "end": v(70.07, -2.4) * mm});
            skLineSegment(sketch, "E1.97.1.3", {"start": v(69.57, -4.6) * mm, "end": v(70.07, -4.6) * mm});
            skLineSegment(sketch, "E1.98.0.0", {"start": v(70.37, 0) * mm, "end": v(70.37, 2.2) * mm});
            skLineSegment(sketch, "E1.98.0.1", {"start": v(70.37, 2.2) * mm, "end": v(70.87, 2.2) * mm});
            skLineSegment(sketch, "E1.98.0.2", {"start": v(70.87, 0) * mm, "end": v(70.87, 2.2) * mm});
            skLineSegment(sketch, "E1.98.0.3", {"start": v(70.37, 0) * mm, "end": v(70.87, 0) * mm});
            skLineSegment(sketch, "E1.98.1.0", {"start": v(70.37, -4.6) * mm, "end": v(70.37, -2.4) * mm});
            skLineSegment(sketch, "E1.98.1.1", {"start": v(70.37, -2.4) * mm, "end": v(70.87, -2.4) * mm});
            skLineSegment(sketch, "E1.98.1.2", {"start": v(70.87, -4.6) * mm, "end": v(70.87, -2.4) * mm});
            skLineSegment(sketch, "E1.98.1.3", {"start": v(70.37, -4.6) * mm, "end": v(70.87, -4.6) * mm});
            skLineSegment(sketch, "E1.99.0.0", {"start": v(71.17, 0) * mm, "end": v(71.17, 2.2) * mm});
            skLineSegment(sketch, "E1.99.0.1", {"start": v(71.17, 2.2) * mm, "end": v(71.67, 2.2) * mm});
            skLineSegment(sketch, "E1.99.0.2", {"start": v(71.67, 0) * mm, "end": v(71.67, 2.2) * mm});
            skLineSegment(sketch, "E1.99.0.3", {"start": v(71.17, 0) * mm, "end": v(71.67, 0) * mm});
            skLineSegment(sketch, "E1.99.1.0", {"start": v(71.17, -4.6) * mm, "end": v(71.17, -2.4) * mm});
            skLineSegment(sketch, "E1.99.1.1", {"start": v(71.17, -2.4) * mm, "end": v(71.67, -2.4) * mm});
            skLineSegment(sketch, "E1.99.1.2", {"start": v(71.67, -4.6) * mm, "end": v(71.67, -2.4) * mm});
            skLineSegment(sketch, "E1.99.1.3", {"start": v(71.17, -4.6) * mm, "end": v(71.67, -4.6) * mm});
            skLineSegment(sketch, "E1.direction1", {"start": v(-8.03, 0) * mm, "end": v(-7.23, 0) * mm, "construction": true});
            skLineSegment(sketch, "E1.direction2", {"start": v(-8.03, 0) * mm, "end": v(-8.03, -4.6) * mm, "construction": true});
            skSolve(sketch);
        }
        {
            var Q0;
            Q0=makeQuery(id+"F0.imprint","IMPRINT",FACE,{"disambiguationData":[TD([[makeQuery(id+"F0.imprint","IMPRINT",EDGE,{"derivedFrom":sQuery(id+"F0.wireOp",EDGE,"E0.bottom")}),1.0]])]});
            var sketch = newSketch(context, id + "F1", { "sketchPlane" : qUnion([Q0])});
            skLineSegment(sketch, "E2.bottom", {"start": v(-16.69, -7.36) * mm, "end": v(-16.29, -7.36) * mm});
            skLineSegment(sketch, "E2.top", {"start": v(-16.69, -5.16) * mm, "end": v(-16.29, -5.16) * mm});
            skLineSegment(sketch, "E2.left", {"start": v(-16.69, -7.36) * mm, "end": v(-16.69, -5.16) * mm});
            skLineSegment(sketch, "E2.right", {"start": v(-16.29, -7.36) * mm, "end": v(-16.29, -5.16) * mm});
            skLineSegment(sketch, "E3.0.1.0", {"start": v(-16.69, -2.56) * mm, "end": v(-16.29, -2.56) * mm});
            skLineSegment(sketch, "E3.0.1.1", {"start": v(-16.69, -4.76) * mm, "end": v(-16.69, -2.56) * mm});
            skLineSegment(sketch, "E3.0.1.2", {"start": v(-16.69, -4.76) * mm, "end": v(-16.29, -4.76) * mm});
            skLineSegment(sketch, "E3.0.1.3", {"start": v(-16.29, -4.76) * mm, "end": v(-16.29, -2.56) * mm});
            skLineSegment(sketch, "E3.1.0.0", {"start": v(-15.89, -5.16) * mm, "end": v(-15.49, -5.16) * mm});
            skLineSegment(sketch, "E3.1.0.1", {"start": v(-15.89, -7.36) * mm, "end": v(-15.89, -5.16) * mm});
            skLineSegment(sketch, "E3.1.0.2", {"start": v(-15.89, -7.36) * mm, "end": v(-15.49, -7.36) * mm});
            skLineSegment(sketch, "E3.1.0.3", {"start": v(-15.49, -7.36) * mm, "end": v(-15.49, -5.16) * mm});
            skLineSegment(sketch, "E3.1.1.0", {"start": v(-15.89, -2.56) * mm, "end": v(-15.49, -2.56) * mm});
            skLineSegment(sketch, "E3.1.1.1", {"start": v(-15.89, -4.76) * mm, "end": v(-15.89, -2.56) * mm});
            skLineSegment(sketch, "E3.1.1.2", {"start": v(-15.89, -4.76) * mm, "end": v(-15.49, -4.76) * mm});
            skLineSegment(sketch, "E3.1.1.3", {"start": v(-15.49, -4.76) * mm, "end": v(-15.49, -2.56) * mm});
            skLineSegment(sketch, "E3.2.0.0", {"start": v(-15.09, -5.16) * mm, "end": v(-14.69, -5.16) * mm});
            skLineSegment(sketch, "E3.2.0.1", {"start": v(-15.09, -7.36) * mm, "end": v(-15.09, -5.16) * mm});
            skLineSegment(sketch, "E3.2.0.2", {"start": v(-15.09, -7.36) * mm, "end": v(-14.69, -7.36) * mm});
            skLineSegment(sketch, "E3.2.0.3", {"start": v(-14.69, -7.36) * mm, "end": v(-14.69, -5.16) * mm});
            skLineSegment(sketch, "E3.2.1.0", {"start": v(-15.09, -2.56) * mm, "end": v(-14.69, -2.56) * mm});
            skLineSegment(sketch, "E3.2.1.1", {"start": v(-15.09, -4.76) * mm, "end": v(-15.09, -2.56) * mm});
            skLineSegment(sketch, "E3.2.1.2", {"start": v(-15.09, -4.76) * mm, "end": v(-14.69, -4.76) * mm});
            skLineSegment(sketch, "E3.2.1.3", {"start": v(-14.69, -4.76) * mm, "end": v(-14.69, -2.56) * mm});
            skLineSegment(sketch, "E3.3.0.0", {"start": v(-14.29, -5.16) * mm, "end": v(-13.89, -5.16) * mm});
            skLineSegment(sketch, "E3.3.0.1", {"start": v(-14.29, -7.36) * mm, "end": v(-14.29, -5.16) * mm});
            skLineSegment(sketch, "E3.3.0.2", {"start": v(-14.29, -7.36) * mm, "end": v(-13.89, -7.36) * mm});
            skLineSegment(sketch, "E3.3.0.3", {"start": v(-13.89, -7.36) * mm, "end": v(-13.89, -5.16) * mm});
            skLineSegment(sketch, "E3.3.1.0", {"start": v(-14.29, -2.56) * mm, "end": v(-13.89, -2.56) * mm});
            skLineSegment(sketch, "E3.3.1.1", {"start": v(-14.29, -4.76) * mm, "end": v(-14.29, -2.56) * mm});
            skLineSegment(sketch, "E3.3.1.2", {"start": v(-14.29, -4.76) * mm, "end": v(-13.89, -4.76) * mm});
            skLineSegment(sketch, "E3.3.1.3", {"start": v(-13.89, -4.76) * mm, "end": v(-13.89, -2.56) * mm});
            skLineSegment(sketch, "E3.4.0.0", {"start": v(-13.49, -5.16) * mm, "end": v(-13.09, -5.16) * mm});
            skLineSegment(sketch, "E3.4.0.1", {"start": v(-13.49, -7.36) * mm, "end": v(-13.49, -5.16) * mm});
            skLineSegment(sketch, "E3.4.0.2", {"start": v(-13.49, -7.36) * mm, "end": v(-13.09, -7.36) * mm});
            skLineSegment(sketch, "E3.4.0.3", {"start": v(-13.09, -7.36) * mm, "end": v(-13.09, -5.16) * mm});
            skLineSegment(sketch, "E3.4.1.0", {"start": v(-13.49, -2.56) * mm, "end": v(-13.09, -2.56) * mm});
            skLineSegment(sketch, "E3.4.1.1", {"start": v(-13.49, -4.76) * mm, "end": v(-13.49, -2.56) * mm});
            skLineSegment(sketch, "E3.4.1.2", {"start": v(-13.49, -4.76) * mm, "end": v(-13.09, -4.76) * mm});
            skLineSegment(sketch, "E3.4.1.3", {"start": v(-13.09, -4.76) * mm, "end": v(-13.09, -2.56) * mm});
            skLineSegment(sketch, "E3.5.0.0", {"start": v(-12.69, -5.16) * mm, "end": v(-12.29, -5.16) * mm});
            skLineSegment(sketch, "E3.5.0.1", {"start": v(-12.69, -7.36) * mm, "end": v(-12.69, -5.16) * mm});
            skLineSegment(sketch, "E3.5.0.2", {"start": v(-12.69, -7.36) * mm, "end": v(-12.29, -7.36) * mm});
            skLineSegment(sketch, "E3.5.0.3", {"start": v(-12.29, -7.36) * mm, "end": v(-12.29, -5.16) * mm});
            skLineSegment(sketch, "E3.5.1.0", {"start": v(-12.69, -2.56) * mm, "end": v(-12.29, -2.56) * mm});
            skLineSegment(sketch, "E3.5.1.1", {"start": v(-12.69, -4.76) * mm, "end": v(-12.69, -2.56) * mm});
            skLineSegment(sketch, "E3.5.1.2", {"start": v(-12.69, -4.76) * mm, "end": v(-12.29, -4.76) * mm});
            skLineSegment(sketch, "E3.5.1.3", {"start": v(-12.29, -4.76) * mm, "end": v(-12.29, -2.56) * mm});
            skLineSegment(sketch, "E3.6.0.0", {"start": v(-11.89, -5.16) * mm, "end": v(-11.49, -5.16) * mm});
            skLineSegment(sketch, "E3.6.0.1", {"start": v(-11.89, -7.36) * mm, "end": v(-11.89, -5.16) * mm});
            skLineSegment(sketch, "E3.6.0.2", {"start": v(-11.89, -7.36) * mm, "end": v(-11.49, -7.36) * mm});
            skLineSegment(sketch, "E3.6.0.3", {"start": v(-11.49, -7.36) * mm, "end": v(-11.49, -5.16) * mm});
            skLineSegment(sketch, "E3.6.1.0", {"start": v(-11.89, -2.56) * mm, "end": v(-11.49, -2.56) * mm});
            skLineSegment(sketch, "E3.6.1.1", {"start": v(-11.89, -4.76) * mm, "end": v(-11.89, -2.56) * mm});
            skLineSegment(sketch, "E3.6.1.2", {"start": v(-11.89, -4.76) * mm, "end": v(-11.49, -4.76) * mm});
            skLineSegment(sketch, "E3.6.1.3", {"start": v(-11.49, -4.76) * mm, "end": v(-11.49, -2.56) * mm});
            skLineSegment(sketch, "E3.7.0.0", {"start": v(-11.09, -5.16) * mm, "end": v(-10.69, -5.16) * mm});
            skLineSegment(sketch, "E3.7.0.1", {"start": v(-11.09, -7.36) * mm, "end": v(-11.09, -5.16) * mm});
            skLineSegment(sketch, "E3.7.0.2", {"start": v(-11.09, -7.36) * mm, "end": v(-10.69, -7.36) * mm});
            skLineSegment(sketch, "E3.7.0.3", {"start": v(-10.69, -7.36) * mm, "end": v(-10.69, -5.16) * mm});
            skLineSegment(sketch, "E3.7.1.0", {"start": v(-11.09, -2.56) * mm, "end": v(-10.69, -2.56) * mm});
            skLineSegment(sketch, "E3.7.1.1", {"start": v(-11.09, -4.76) * mm, "end": v(-11.09, -2.56) * mm});
            skLineSegment(sketch, "E3.7.1.2", {"start": v(-11.09, -4.76) * mm, "end": v(-10.69, -4.76) * mm});
            skLineSegment(sketch, "E3.7.1.3", {"start": v(-10.69, -4.76) * mm, "end": v(-10.69, -2.56) * mm});
            skLineSegment(sketch, "E3.8.0.0", {"start": v(-10.29, -5.16) * mm, "end": v(-9.89, -5.16) * mm});
            skLineSegment(sketch, "E3.8.0.1", {"start": v(-10.29, -7.36) * mm, "end": v(-10.29, -5.16) * mm});
            skLineSegment(sketch, "E3.8.0.2", {"start": v(-10.29, -7.36) * mm, "end": v(-9.89, -7.36) * mm});
            skLineSegment(sketch, "E3.8.0.3", {"start": v(-9.89, -7.36) * mm, "end": v(-9.89, -5.16) * mm});
            skLineSegment(sketch, "E3.8.1.0", {"start": v(-10.29, -2.56) * mm, "end": v(-9.89, -2.56) * mm});
            skLineSegment(sketch, "E3.8.1.1", {"start": v(-10.29, -4.76) * mm, "end": v(-10.29, -2.56) * mm});
            skLineSegment(sketch, "E3.8.1.2", {"start": v(-10.29, -4.76) * mm, "end": v(-9.89, -4.76) * mm});
            skLineSegment(sketch, "E3.8.1.3", {"start": v(-9.89, -4.76) * mm, "end": v(-9.89, -2.56) * mm});
            skLineSegment(sketch, "E3.9.0.0", {"start": v(-9.49, -5.16) * mm, "end": v(-9.09, -5.16) * mm});
            skLineSegment(sketch, "E3.9.0.1", {"start": v(-9.49, -7.36) * mm, "end": v(-9.49, -5.16) * mm});
            skLineSegment(sketch, "E3.9.0.2", {"start": v(-9.49, -7.36) * mm, "end": v(-9.09, -7.36) * mm});
            skLineSegment(sketch, "E3.9.0.3", {"start": v(-9.09, -7.36) * mm, "end": v(-9.09, -5.16) * mm});
            skLineSegment(sketch, "E3.9.1.0", {"start": v(-9.49, -2.56) * mm, "end": v(-9.09, -2.56) * mm});
            skLineSegment(sketch, "E3.9.1.1", {"start": v(-9.49, -4.76) * mm, "end": v(-9.49, -2.56) * mm});
            skLineSegment(sketch, "E3.9.1.2", {"start": v(-9.49, -4.76) * mm, "end": v(-9.09, -4.76) * mm});
            skLineSegment(sketch, "E3.9.1.3", {"start": v(-9.09, -4.76) * mm, "end": v(-9.09, -2.56) * mm});
            skLineSegment(sketch, "E3.10.0.0", {"start": v(-8.69, -5.16) * mm, "end": v(-8.29, -5.16) * mm});
            skLineSegment(sketch, "E3.10.0.1", {"start": v(-8.69, -7.36) * mm, "end": v(-8.69, -5.16) * mm});
            skLineSegment(sketch, "E3.10.0.2", {"start": v(-8.69, -7.36) * mm, "end": v(-8.29, -7.36) * mm});
            skLineSegment(sketch, "E3.10.0.3", {"start": v(-8.29, -7.36) * mm, "end": v(-8.29, -5.16) * mm});
            skLineSegment(sketch, "E3.10.1.0", {"start": v(-8.69, -2.56) * mm, "end": v(-8.29, -2.56) * mm});
            skLineSegment(sketch, "E3.10.1.1", {"start": v(-8.69, -4.76) * mm, "end": v(-8.69, -2.56) * mm});
            skLineSegment(sketch, "E3.10.1.2", {"start": v(-8.69, -4.76) * mm, "end": v(-8.29, -4.76) * mm});
            skLineSegment(sketch, "E3.10.1.3", {"start": v(-8.29, -4.76) * mm, "end": v(-8.29, -2.56) * mm});
            skLineSegment(sketch, "E3.11.0.0", {"start": v(-7.89, -5.16) * mm, "end": v(-7.49, -5.16) * mm});
            skLineSegment(sketch, "E3.11.0.1", {"start": v(-7.89, -7.36) * mm, "end": v(-7.89, -5.16) * mm});
            skLineSegment(sketch, "E3.11.0.2", {"start": v(-7.89, -7.36) * mm, "end": v(-7.49, -7.36) * mm});
            skLineSegment(sketch, "E3.11.0.3", {"start": v(-7.49, -7.36) * mm, "end": v(-7.49, -5.16) * mm});
            skLineSegment(sketch, "E3.11.1.0", {"start": v(-7.89, -2.56) * mm, "end": v(-7.49, -2.56) * mm});
            skLineSegment(sketch, "E3.11.1.1", {"start": v(-7.89, -4.76) * mm, "end": v(-7.89, -2.56) * mm});
            skLineSegment(sketch, "E3.11.1.2", {"start": v(-7.89, -4.76) * mm, "end": v(-7.49, -4.76) * mm});
            skLineSegment(sketch, "E3.11.1.3", {"start": v(-7.49, -4.76) * mm, "end": v(-7.49, -2.56) * mm});
            skLineSegment(sketch, "E3.12.0.0", {"start": v(-7.09, -5.16) * mm, "end": v(-6.69, -5.16) * mm});
            skLineSegment(sketch, "E3.12.0.1", {"start": v(-7.09, -7.36) * mm, "end": v(-7.09, -5.16) * mm});
            skLineSegment(sketch, "E3.12.0.2", {"start": v(-7.09, -7.36) * mm, "end": v(-6.69, -7.36) * mm});
            skLineSegment(sketch, "E3.12.0.3", {"start": v(-6.69, -7.36) * mm, "end": v(-6.69, -5.16) * mm});
            skLineSegment(sketch, "E3.12.1.0", {"start": v(-7.09, -2.56) * mm, "end": v(-6.69, -2.56) * mm});
            skLineSegment(sketch, "E3.12.1.1", {"start": v(-7.09, -4.76) * mm, "end": v(-7.09, -2.56) * mm});
            skLineSegment(sketch, "E3.12.1.2", {"start": v(-7.09, -4.76) * mm, "end": v(-6.69, -4.76) * mm});
            skLineSegment(sketch, "E3.12.1.3", {"start": v(-6.69, -4.76) * mm, "end": v(-6.69, -2.56) * mm});
            skLineSegment(sketch, "E3.13.0.0", {"start": v(-6.29, -5.16) * mm, "end": v(-5.89, -5.16) * mm});
            skLineSegment(sketch, "E3.13.0.1", {"start": v(-6.29, -7.36) * mm, "end": v(-6.29, -5.16) * mm});
            skLineSegment(sketch, "E3.13.0.2", {"start": v(-6.29, -7.36) * mm, "end": v(-5.89, -7.36) * mm});
            skLineSegment(sketch, "E3.13.0.3", {"start": v(-5.89, -7.36) * mm, "end": v(-5.89, -5.16) * mm});
            skLineSegment(sketch, "E3.13.1.0", {"start": v(-6.29, -2.56) * mm, "end": v(-5.89, -2.56) * mm});
            skLineSegment(sketch, "E3.13.1.1", {"start": v(-6.29, -4.76) * mm, "end": v(-6.29, -2.56) * mm});
            skLineSegment(sketch, "E3.13.1.2", {"start": v(-6.29, -4.76) * mm, "end": v(-5.89, -4.76) * mm});
            skLineSegment(sketch, "E3.13.1.3", {"start": v(-5.89, -4.76) * mm, "end": v(-5.89, -2.56) * mm});
            skLineSegment(sketch, "E3.14.0.0", {"start": v(-5.49, -5.16) * mm, "end": v(-5.09, -5.16) * mm});
            skLineSegment(sketch, "E3.14.0.1", {"start": v(-5.49, -7.36) * mm, "end": v(-5.49, -5.16) * mm});
            skLineSegment(sketch, "E3.14.0.2", {"start": v(-5.49, -7.36) * mm, "end": v(-5.09, -7.36) * mm});
            skLineSegment(sketch, "E3.14.0.3", {"start": v(-5.09, -7.36) * mm, "end": v(-5.09, -5.16) * mm});
            skLineSegment(sketch, "E3.14.1.0", {"start": v(-5.49, -2.56) * mm, "end": v(-5.09, -2.56) * mm});
            skLineSegment(sketch, "E3.14.1.1", {"start": v(-5.49, -4.76) * mm, "end": v(-5.49, -2.56) * mm});
            skLineSegment(sketch, "E3.14.1.2", {"start": v(-5.49, -4.76) * mm, "end": v(-5.09, -4.76) * mm});
            skLineSegment(sketch, "E3.14.1.3", {"start": v(-5.09, -4.76) * mm, "end": v(-5.09, -2.56) * mm});
            skLineSegment(sketch, "E3.15.0.0", {"start": v(-4.69, -5.16) * mm, "end": v(-4.29, -5.16) * mm});
            skLineSegment(sketch, "E3.15.0.1", {"start": v(-4.69, -7.36) * mm, "end": v(-4.69, -5.16) * mm});
            skLineSegment(sketch, "E3.15.0.2", {"start": v(-4.69, -7.36) * mm, "end": v(-4.29, -7.36) * mm});
            skLineSegment(sketch, "E3.15.0.3", {"start": v(-4.29, -7.36) * mm, "end": v(-4.29, -5.16) * mm});
            skLineSegment(sketch, "E3.15.1.0", {"start": v(-4.69, -2.56) * mm, "end": v(-4.29, -2.56) * mm});
            skLineSegment(sketch, "E3.15.1.1", {"start": v(-4.69, -4.76) * mm, "end": v(-4.69, -2.56) * mm});
            skLineSegment(sketch, "E3.15.1.2", {"start": v(-4.69, -4.76) * mm, "end": v(-4.29, -4.76) * mm});
            skLineSegment(sketch, "E3.15.1.3", {"start": v(-4.29, -4.76) * mm, "end": v(-4.29, -2.56) * mm});
            skLineSegment(sketch, "E3.16.0.0", {"start": v(-3.89, -5.16) * mm, "end": v(-3.49, -5.16) * mm});
            skLineSegment(sketch, "E3.16.0.1", {"start": v(-3.89, -7.36) * mm, "end": v(-3.89, -5.16) * mm});
            skLineSegment(sketch, "E3.16.0.2", {"start": v(-3.89, -7.36) * mm, "end": v(-3.49, -7.36) * mm});
            skLineSegment(sketch, "E3.16.0.3", {"start": v(-3.49, -7.36) * mm, "end": v(-3.49, -5.16) * mm});
            skLineSegment(sketch, "E3.16.1.0", {"start": v(-3.89, -2.56) * mm, "end": v(-3.49, -2.56) * mm});
            skLineSegment(sketch, "E3.16.1.1", {"start": v(-3.89, -4.76) * mm, "end": v(-3.89, -2.56) * mm});
            skLineSegment(sketch, "E3.16.1.2", {"start": v(-3.89, -4.76) * mm, "end": v(-3.49, -4.76) * mm});
            skLineSegment(sketch, "E3.16.1.3", {"start": v(-3.49, -4.76) * mm, "end": v(-3.49, -2.56) * mm});
            skLineSegment(sketch, "E3.17.0.0", {"start": v(-3.09, -5.16) * mm, "end": v(-2.69, -5.16) * mm});
            skLineSegment(sketch, "E3.17.0.1", {"start": v(-3.09, -7.36) * mm, "end": v(-3.09, -5.16) * mm});
            skLineSegment(sketch, "E3.17.0.2", {"start": v(-3.09, -7.36) * mm, "end": v(-2.69, -7.36) * mm});
            skLineSegment(sketch, "E3.17.0.3", {"start": v(-2.69, -7.36) * mm, "end": v(-2.69, -5.16) * mm});
            skLineSegment(sketch, "E3.17.1.0", {"start": v(-3.09, -2.56) * mm, "end": v(-2.69, -2.56) * mm});
            skLineSegment(sketch, "E3.17.1.1", {"start": v(-3.09, -4.76) * mm, "end": v(-3.09, -2.56) * mm});
            skLineSegment(sketch, "E3.17.1.2", {"start": v(-3.09, -4.76) * mm, "end": v(-2.69, -4.76) * mm});
            skLineSegment(sketch, "E3.17.1.3", {"start": v(-2.69, -4.76) * mm, "end": v(-2.69, -2.56) * mm});
            skLineSegment(sketch, "E3.18.0.0", {"start": v(-2.29, -5.16) * mm, "end": v(-1.89, -5.16) * mm});
            skLineSegment(sketch, "E3.18.0.1", {"start": v(-2.29, -7.36) * mm, "end": v(-2.29, -5.16) * mm});
            skLineSegment(sketch, "E3.18.0.2", {"start": v(-2.29, -7.36) * mm, "end": v(-1.89, -7.36) * mm});
            skLineSegment(sketch, "E3.18.0.3", {"start": v(-1.89, -7.36) * mm, "end": v(-1.89, -5.16) * mm});
            skLineSegment(sketch, "E3.18.1.0", {"start": v(-2.29, -2.56) * mm, "end": v(-1.89, -2.56) * mm});
            skLineSegment(sketch, "E3.18.1.1", {"start": v(-2.29, -4.76) * mm, "end": v(-2.29, -2.56) * mm});
            skLineSegment(sketch, "E3.18.1.2", {"start": v(-2.29, -4.76) * mm, "end": v(-1.89, -4.76) * mm});
            skLineSegment(sketch, "E3.18.1.3", {"start": v(-1.89, -4.76) * mm, "end": v(-1.89, -2.56) * mm});
            skLineSegment(sketch, "E3.19.0.0", {"start": v(-1.49, -5.16) * mm, "end": v(-1.09, -5.16) * mm});
            skLineSegment(sketch, "E3.19.0.1", {"start": v(-1.49, -7.36) * mm, "end": v(-1.49, -5.16) * mm});
            skLineSegment(sketch, "E3.19.0.2", {"start": v(-1.49, -7.36) * mm, "end": v(-1.09, -7.36) * mm});
            skLineSegment(sketch, "E3.19.0.3", {"start": v(-1.09, -7.36) * mm, "end": v(-1.09, -5.16) * mm});
            skLineSegment(sketch, "E3.19.1.0", {"start": v(-1.49, -2.56) * mm, "end": v(-1.09, -2.56) * mm});
            skLineSegment(sketch, "E3.19.1.1", {"start": v(-1.49, -4.76) * mm, "end": v(-1.49, -2.56) * mm});
            skLineSegment(sketch, "E3.19.1.2", {"start": v(-1.49, -4.76) * mm, "end": v(-1.09, -4.76) * mm});
            skLineSegment(sketch, "E3.19.1.3", {"start": v(-1.09, -4.76) * mm, "end": v(-1.09, -2.56) * mm});
            skLineSegment(sketch, "E3.20.0.0", {"start": v(-0.69, -5.16) * mm, "end": v(-0.29, -5.16) * mm});
            skLineSegment(sketch, "E3.20.0.1", {"start": v(-0.69, -7.36) * mm, "end": v(-0.69, -5.16) * mm});
            skLineSegment(sketch, "E3.20.0.2", {"start": v(-0.69, -7.36) * mm, "end": v(-0.29, -7.36) * mm});
            skLineSegment(sketch, "E3.20.0.3", {"start": v(-0.29, -7.36) * mm, "end": v(-0.29, -5.16) * mm});
            skLineSegment(sketch, "E3.20.1.0", {"start": v(-0.69, -2.56) * mm, "end": v(-0.29, -2.56) * mm});
            skLineSegment(sketch, "E3.20.1.1", {"start": v(-0.69, -4.76) * mm, "end": v(-0.69, -2.56) * mm});
            skLineSegment(sketch, "E3.20.1.2", {"start": v(-0.69, -4.76) * mm, "end": v(-0.29, -4.76) * mm});
            skLineSegment(sketch, "E3.20.1.3", {"start": v(-0.29, -4.76) * mm, "end": v(-0.29, -2.56) * mm});
            skLineSegment(sketch, "E3.21.0.0", {"start": v(0.11, -5.16) * mm, "end": v(0.51, -5.16) * mm});
            skLineSegment(sketch, "E3.21.0.1", {"start": v(0.11, -7.36) * mm, "end": v(0.11, -5.16) * mm});
            skLineSegment(sketch, "E3.21.0.2", {"start": v(0.11, -7.36) * mm, "end": v(0.51, -7.36) * mm});
            skLineSegment(sketch, "E3.21.0.3", {"start": v(0.51, -7.36) * mm, "end": v(0.51, -5.16) * mm});
            skLineSegment(sketch, "E3.21.1.0", {"start": v(0.11, -2.56) * mm, "end": v(0.51, -2.56) * mm});
            skLineSegment(sketch, "E3.21.1.1", {"start": v(0.11, -4.76) * mm, "end": v(0.11, -2.56) * mm});
            skLineSegment(sketch, "E3.21.1.2", {"start": v(0.11, -4.76) * mm, "end": v(0.51, -4.76) * mm});
            skLineSegment(sketch, "E3.21.1.3", {"start": v(0.51, -4.76) * mm, "end": v(0.51, -2.56) * mm});
            skLineSegment(sketch, "E3.22.0.0", {"start": v(0.91, -5.16) * mm, "end": v(1.31, -5.16) * mm});
            skLineSegment(sketch, "E3.22.0.1", {"start": v(0.91, -7.36) * mm, "end": v(0.91, -5.16) * mm});
            skLineSegment(sketch, "E3.22.0.2", {"start": v(0.91, -7.36) * mm, "end": v(1.31, -7.36) * mm});
            skLineSegment(sketch, "E3.22.0.3", {"start": v(1.31, -7.36) * mm, "end": v(1.31, -5.16) * mm});
            skLineSegment(sketch, "E3.22.1.0", {"start": v(0.91, -2.56) * mm, "end": v(1.31, -2.56) * mm});
            skLineSegment(sketch, "E3.22.1.1", {"start": v(0.91, -4.76) * mm, "end": v(0.91, -2.56) * mm});
            skLineSegment(sketch, "E3.22.1.2", {"start": v(0.91, -4.76) * mm, "end": v(1.31, -4.76) * mm});
            skLineSegment(sketch, "E3.22.1.3", {"start": v(1.31, -4.76) * mm, "end": v(1.31, -2.56) * mm});
            skLineSegment(sketch, "E3.23.0.0", {"start": v(1.71, -5.16) * mm, "end": v(2.11, -5.16) * mm});
            skLineSegment(sketch, "E3.23.0.1", {"start": v(1.71, -7.36) * mm, "end": v(1.71, -5.16) * mm});
            skLineSegment(sketch, "E3.23.0.2", {"start": v(1.71, -7.36) * mm, "end": v(2.11, -7.36) * mm});
            skLineSegment(sketch, "E3.23.0.3", {"start": v(2.11, -7.36) * mm, "end": v(2.11, -5.16) * mm});
            skLineSegment(sketch, "E3.23.1.0", {"start": v(1.71, -2.56) * mm, "end": v(2.11, -2.56) * mm});
            skLineSegment(sketch, "E3.23.1.1", {"start": v(1.71, -4.76) * mm, "end": v(1.71, -2.56) * mm});
            skLineSegment(sketch, "E3.23.1.2", {"start": v(1.71, -4.76) * mm, "end": v(2.11, -4.76) * mm});
            skLineSegment(sketch, "E3.23.1.3", {"start": v(2.11, -4.76) * mm, "end": v(2.11, -2.56) * mm});
            skLineSegment(sketch, "E3.24.0.0", {"start": v(2.51, -5.16) * mm, "end": v(2.91, -5.16) * mm});
            skLineSegment(sketch, "E3.24.0.1", {"start": v(2.51, -7.36) * mm, "end": v(2.51, -5.16) * mm});
            skLineSegment(sketch, "E3.24.0.2", {"start": v(2.51, -7.36) * mm, "end": v(2.91, -7.36) * mm});
            skLineSegment(sketch, "E3.24.0.3", {"start": v(2.91, -7.36) * mm, "end": v(2.91, -5.16) * mm});
            skLineSegment(sketch, "E3.24.1.0", {"start": v(2.51, -2.56) * mm, "end": v(2.91, -2.56) * mm});
            skLineSegment(sketch, "E3.24.1.1", {"start": v(2.51, -4.76) * mm, "end": v(2.51, -2.56) * mm});
            skLineSegment(sketch, "E3.24.1.2", {"start": v(2.51, -4.76) * mm, "end": v(2.91, -4.76) * mm});
            skLineSegment(sketch, "E3.24.1.3", {"start": v(2.91, -4.76) * mm, "end": v(2.91, -2.56) * mm});
            skLineSegment(sketch, "E3.direction1", {"start": v(-16.69, -5.16) * mm, "end": v(-15.89, -5.16) * mm, "construction": true});
            skLineSegment(sketch, "E3.direction2", {"start": v(-16.69, -5.16) * mm, "end": v(-16.69, -2.56) * mm, "construction": true});
            skLineSegment(sketch, "E4.bottom", {"start": v(-17.11, -1.7) * mm, "end": v(3.38, -1.7) * mm});
            skLineSegment(sketch, "E4.top", {"start": v(-17.11, -8.41) * mm, "end": v(3.38, -8.41) * mm});
            skLineSegment(sketch, "E4.left", {"start": v(-17.11, -1.7) * mm, "end": v(-17.11, -8.41) * mm});
            skLineSegment(sketch, "E4.right", {"start": v(3.38, -1.7) * mm, "end": v(3.38, -8.41) * mm});
            skSolve(sketch);
        }
        {
            var Q0;
            Q0=makeQuery(id+"F1.imprint","IMPRINT",FACE,{"disambiguationData":[TD([[makeQuery(id+"F1.imprint","IMPRINT",EDGE,{"derivedFrom":sQuery(id+"F1.wireOp",EDGE,"E2.bottom")}),-1.0]])]});
            extrude(context, id + "F2", {"entities" : qUnion([Q0]), "depth" : 1 * mm, "offsetDistance" : 25 * mm});
        }
    });
